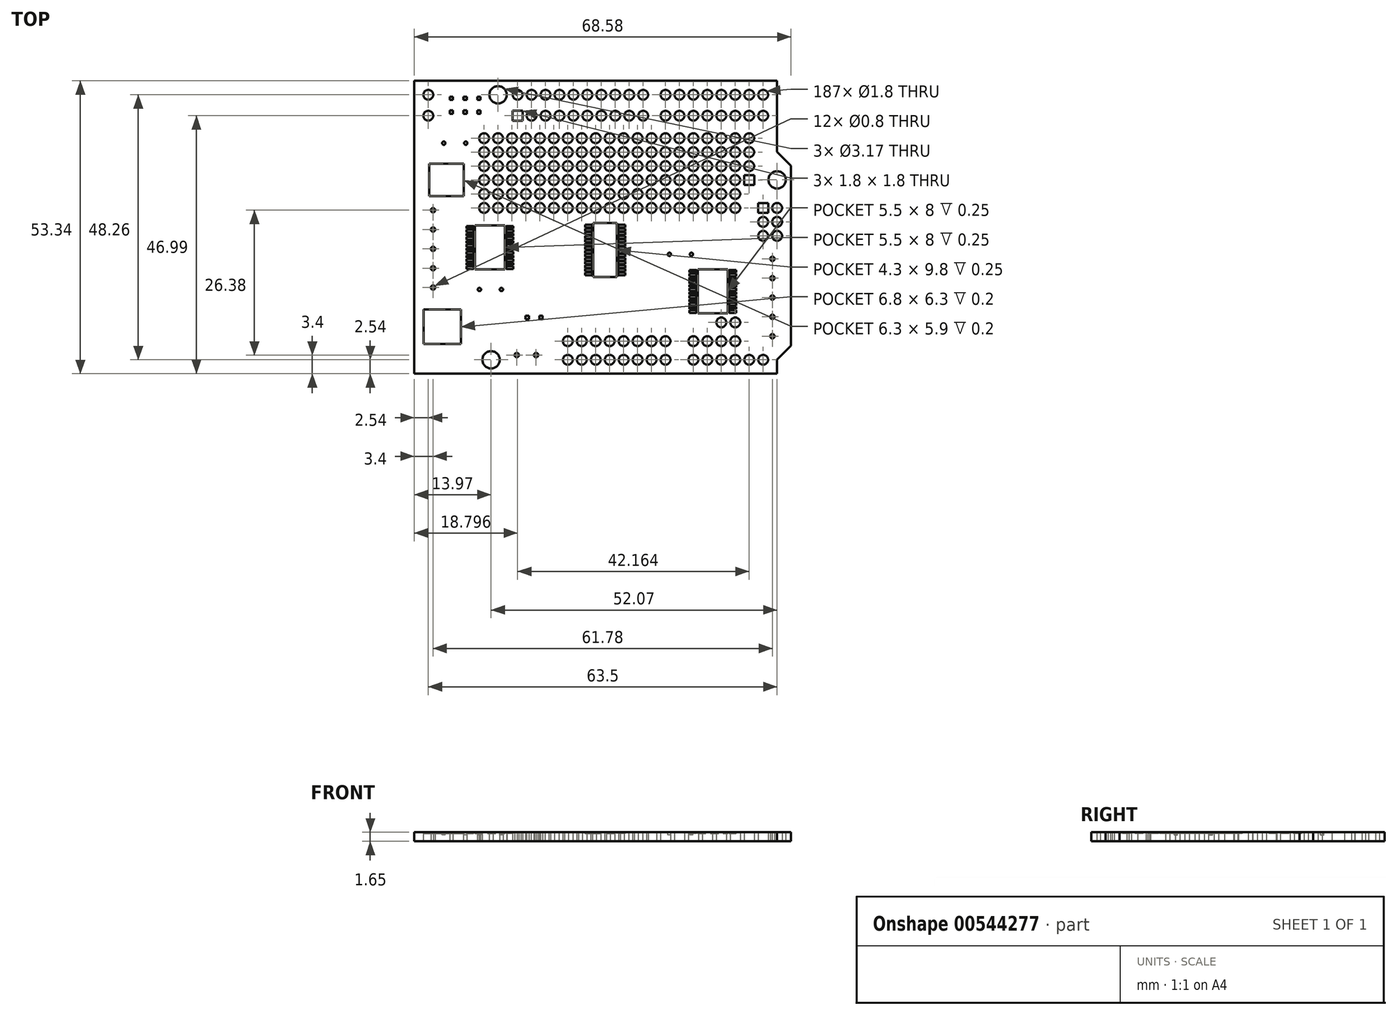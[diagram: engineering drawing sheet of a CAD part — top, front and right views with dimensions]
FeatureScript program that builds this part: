
annotation { "Feature Type Name" : "Feature", "Feature Type Description" : "" }
export const myFeature = defineFeature(function(context is Context, id is Id, definition is map)
    precondition{}
    {
        {
            var Q0;
            Q0=qCreatedBy(makeId("Top.planeOp"),FACE);
            var sketch = newSketch(context, id + "F0", { "sketchPlane" : qUnion([Q0])});
            skLineSegment(sketch, "E0.bottom", {"start": v(0, 0) * mm, "end": v(66.04, 0) * mm});
            skLineSegment(sketch, "E0.top", {"start": v(0, 53.34) * mm, "end": v(66.04, 53.34) * mm});
            skLineSegment(sketch, "E0.left", {"start": v(0, 0) * mm, "end": v(0, 53.34) * mm});
            skLineSegment(sketch, "E0.right", {"start": v(66.04, 0) * mm, "end": v(66.04, 2.54) * mm});
            skLineSegment(sketch, "E1", {"start": v(66.04, 40.39) * mm, "end": v(68.58, 37.85) * mm});
            skLineSegment(sketch, "E2", {"start": v(68.58, 37.85) * mm, "end": v(68.58, 5.08) * mm});
            skLineSegment(sketch, "E3", {"start": v(68.58, 5.08) * mm, "end": v(66.04, 2.54) * mm});
            skLineSegment(sketch, "E4.trimOffspring", {"start": v(66.04, 40.39) * mm, "end": v(66.04, 53.34) * mm});
            skCircle(sketch, "E5", {"center": v(15.24, 50.8) * mm, "radius": 1.59 * mm});
            skCircle(sketch, "E6", {"center": v(13.97, 2.54) * mm, "radius": 1.59 * mm});
            skCircle(sketch, "E7", {"center": v(66.04, 35.3) * mm, "radius": 1.59 * mm});
            skLineSegment(sketch, "E8", {"start": v(0, 50.8) * mm, "end": v(66.04, 50.8) * mm, "construction": true});
            skCircle(sketch, "E9", {"center": v(63.5, 50.8) * mm, "radius": 0.9 * mm});
            skCircle(sketch, "E10.1.0.0", {"center": v(60.96, 50.8) * mm, "radius": 0.9 * mm});
            skCircle(sketch, "E10.2.0.0", {"center": v(58.42, 50.8) * mm, "radius": 0.9 * mm});
            skCircle(sketch, "E10.3.0.0", {"center": v(55.88, 50.8) * mm, "radius": 0.9 * mm});
            skCircle(sketch, "E10.4.0.0", {"center": v(53.34, 50.8) * mm, "radius": 0.9 * mm});
            skCircle(sketch, "E10.5.0.0", {"center": v(50.8, 50.8) * mm, "radius": 0.9 * mm});
            skCircle(sketch, "E10.6.0.0", {"center": v(48.26, 50.8) * mm, "radius": 0.9 * mm});
            skCircle(sketch, "E10.7.0.0", {"center": v(45.72, 50.8) * mm, "radius": 0.9 * mm});
            skLineSegment(sketch, "E10.direction1", {"start": v(63.5, 50.8) * mm, "end": v(60.96, 50.8) * mm, "construction": true});
            skCircle(sketch, "E11", {"center": v(41.66, 50.8) * mm, "radius": 0.9 * mm});
            skCircle(sketch, "E12.1.0.0", {"center": v(39.12, 50.8) * mm, "radius": 0.9 * mm});
            skCircle(sketch, "E12.2.0.0", {"center": v(36.58, 50.8) * mm, "radius": 0.9 * mm});
            skCircle(sketch, "E12.3.0.0", {"center": v(34.04, 50.8) * mm, "radius": 0.9 * mm});
            skCircle(sketch, "E12.4.0.0", {"center": v(31.5, 50.8) * mm, "radius": 0.9 * mm});
            skCircle(sketch, "E12.5.0.0", {"center": v(28.96, 50.8) * mm, "radius": 0.9 * mm});
            skCircle(sketch, "E12.6.0.0", {"center": v(26.42, 50.8) * mm, "radius": 0.9 * mm});
            skCircle(sketch, "E12.7.0.0", {"center": v(23.88, 50.8) * mm, "radius": 0.9 * mm});
            skCircle(sketch, "E12.8.0.0", {"center": v(21.34, 50.8) * mm, "radius": 0.9 * mm});
            skCircle(sketch, "E12.9.0.0", {"center": v(18.8, 50.8) * mm, "radius": 0.9 * mm});
            skLineSegment(sketch, "E12.direction1", {"start": v(41.66, 50.8) * mm, "end": v(39.12, 50.8) * mm, "construction": true});
            skLineSegment(sketch, "E13", {"start": v(66.04, 2.54) * mm, "end": v(0, 2.54) * mm, "construction": true});
            skCircle(sketch, "E14", {"center": v(63.5, 2.54) * mm, "radius": 0.9 * mm});
            skCircle(sketch, "E15.1.0.0", {"center": v(60.96, 2.54) * mm, "radius": 0.9 * mm});
            skCircle(sketch, "E15.2.0.0", {"center": v(58.42, 2.54) * mm, "radius": 0.9 * mm});
            skCircle(sketch, "E15.3.0.0", {"center": v(55.88, 2.54) * mm, "radius": 0.9 * mm});
            skCircle(sketch, "E15.4.0.0", {"center": v(53.34, 2.54) * mm, "radius": 0.9 * mm});
            skCircle(sketch, "E15.5.0.0", {"center": v(50.8, 2.54) * mm, "radius": 0.9 * mm});
            skLineSegment(sketch, "E15.direction1", {"start": v(63.5, 2.54) * mm, "end": v(60.96, 2.54) * mm, "construction": true});
            skCircle(sketch, "E16", {"center": v(45.72, 2.54) * mm, "radius": 0.9 * mm});
            skCircle(sketch, "E17.1.0.0", {"center": v(43.18, 2.54) * mm, "radius": 0.9 * mm});
            skCircle(sketch, "E17.2.0.0", {"center": v(40.64, 2.54) * mm, "radius": 0.9 * mm});
            skCircle(sketch, "E17.3.0.0", {"center": v(38.1, 2.54) * mm, "radius": 0.9 * mm});
            skCircle(sketch, "E17.4.0.0", {"center": v(35.56, 2.54) * mm, "radius": 0.9 * mm});
            skCircle(sketch, "E17.5.0.0", {"center": v(33.02, 2.54) * mm, "radius": 0.9 * mm});
            skCircle(sketch, "E17.6.0.0", {"center": v(30.48, 2.54) * mm, "radius": 0.9 * mm});
            skCircle(sketch, "E17.7.0.0", {"center": v(27.94, 2.54) * mm, "radius": 0.9 * mm});
            skLineSegment(sketch, "E17.direction1", {"start": v(45.72, 2.54) * mm, "end": v(43.18, 2.54) * mm, "construction": true});
            skLineSegment(sketch, "E18", {"start": v(0, 46.99) * mm, "end": v(66.04, 46.99) * mm, "construction": true});
            skLineSegment(sketch, "E19.1.0.0", {"start": v(41.66, 46.99) * mm, "end": v(39.12, 46.99) * mm, "construction": true});
            skLineSegment(sketch, "E19.1.0.1", {"start": v(63.5, 46.99) * mm, "end": v(60.96, 46.99) * mm, "construction": true});
            skCircle(sketch, "E19.1.0.2", {"center": v(48.26, 46.99) * mm, "radius": 0.9 * mm});
            skCircle(sketch, "E19.1.0.3", {"center": v(31.5, 47) * mm, "radius": 0.9 * mm});
            skCircle(sketch, "E19.1.0.4", {"center": v(50.8, 46.99) * mm, "radius": 0.9 * mm});
            skCircle(sketch, "E19.1.0.6", {"center": v(34.04, 47) * mm, "radius": 0.9 * mm});
            skCircle(sketch, "E19.1.0.7", {"center": v(23.88, 47) * mm, "radius": 0.9 * mm});
            skCircle(sketch, "E19.1.0.8", {"center": v(53.34, 46.99) * mm, "radius": 0.9 * mm});
            skCircle(sketch, "E19.1.0.9", {"center": v(21.34, 46.99) * mm, "radius": 0.9 * mm});
            skCircle(sketch, "E19.1.0.10", {"center": v(36.58, 47) * mm, "radius": 0.9 * mm});
            skCircle(sketch, "E19.1.0.11", {"center": v(26.42, 47) * mm, "radius": 0.9 * mm});
            skCircle(sketch, "E19.1.0.12", {"center": v(55.88, 47) * mm, "radius": 0.9 * mm});
            skCircle(sketch, "E19.1.0.13", {"center": v(58.42, 47) * mm, "radius": 0.9 * mm});
            skCircle(sketch, "E19.1.0.14", {"center": v(45.72, 46.99) * mm, "radius": 0.9 * mm});
            skCircle(sketch, "E19.1.0.15", {"center": v(28.96, 47) * mm, "radius": 0.9 * mm});
            skCircle(sketch, "E19.1.0.16", {"center": v(39.12, 47) * mm, "radius": 0.9 * mm});
            skCircle(sketch, "E19.1.0.17", {"center": v(41.66, 47) * mm, "radius": 0.9 * mm});
            skCircle(sketch, "E19.1.0.18", {"center": v(63.5, 47) * mm, "radius": 0.9 * mm});
            skCircle(sketch, "E19.1.0.19", {"center": v(60.96, 47) * mm, "radius": 0.9 * mm});
            skLineSegment(sketch, "E19.direction1", {"start": v(18.8, 50.8) * mm, "end": v(18.8, 46.99) * mm, "construction": true});
            skLineSegment(sketch, "E20", {"start": v(68.58, 5.94) * mm, "end": v(0, 5.94) * mm, "construction": true});
            skLineSegment(sketch, "E21.1.0.0", {"start": v(45.72, 5.94) * mm, "end": v(43.18, 5.94) * mm, "construction": true});
            skCircle(sketch, "E21.1.0.1", {"center": v(55.88, 5.94) * mm, "radius": 0.9 * mm});
            skCircle(sketch, "E21.1.0.2", {"center": v(40.64, 5.94) * mm, "radius": 0.9 * mm});
            skCircle(sketch, "E21.1.0.3", {"center": v(58.42, 5.94) * mm, "radius": 0.9 * mm});
            skCircle(sketch, "E21.1.0.4", {"center": v(38.1, 5.94) * mm, "radius": 0.9 * mm});
            skCircle(sketch, "E21.1.0.5", {"center": v(30.48, 5.94) * mm, "radius": 0.9 * mm});
            skCircle(sketch, "E21.1.0.6", {"center": v(33.02, 5.94) * mm, "radius": 0.9 * mm});
            skCircle(sketch, "E21.1.0.7", {"center": v(50.8, 5.94) * mm, "radius": 0.9 * mm});
            skCircle(sketch, "E21.1.0.8", {"center": v(35.56, 5.94) * mm, "radius": 0.9 * mm});
            skCircle(sketch, "E21.1.0.9", {"center": v(53.34, 5.94) * mm, "radius": 0.9 * mm});
            skCircle(sketch, "E21.1.0.10", {"center": v(27.94, 5.94) * mm, "radius": 0.9 * mm});
            skCircle(sketch, "E21.1.0.11", {"center": v(43.18, 5.94) * mm, "radius": 0.9 * mm});
            skCircle(sketch, "E21.1.0.12", {"center": v(45.72, 5.94) * mm, "radius": 0.9 * mm});
            skLineSegment(sketch, "E21.direction1", {"start": v(27.94, 2.54) * mm, "end": v(27.94, 5.94) * mm, "construction": true});
            skLineSegment(sketch, "E22", {"start": v(58.42, 47) * mm, "end": v(58.42, 5.94) * mm, "construction": true});
            skLineSegment(sketch, "E23", {"start": v(0, 30.2) * mm, "end": v(66.04, 30.2) * mm, "construction": true});
            skLineSegment(sketch, "E24", {"start": v(0, 42.9) * mm, "end": v(66.04, 42.9) * mm, "construction": true});
            skCircle(sketch, "E25", {"center": v(58.42, 42.9) * mm, "radius": 0.9 * mm});
            skCircle(sketch, "E26", {"center": v(58.42, 30.2) * mm, "radius": 0.9 * mm});
            skCircle(sketch, "E27", {"center": v(58.42, 40.36) * mm, "radius": 0.9 * mm});
            skCircle(sketch, "E28", {"center": v(58.42, 37.82) * mm, "radius": 0.9 * mm});
            skCircle(sketch, "E29", {"center": v(58.42, 35.28) * mm, "radius": 0.9 * mm});
            skCircle(sketch, "E30", {"center": v(58.42, 32.74) * mm, "radius": 0.9 * mm});
            skCircle(sketch, "E31.1.0.0", {"center": v(55.88, 35.28) * mm, "radius": 0.9 * mm});
            skCircle(sketch, "E31.1.0.1", {"center": v(55.88, 32.74) * mm, "radius": 0.9 * mm});
            skCircle(sketch, "E31.1.0.2", {"center": v(55.88, 37.82) * mm, "radius": 0.9 * mm});
            skCircle(sketch, "E31.1.0.3", {"center": v(55.88, 40.36) * mm, "radius": 0.9 * mm});
            skCircle(sketch, "E31.1.0.4", {"center": v(55.88, 30.2) * mm, "radius": 0.9 * mm});
            skCircle(sketch, "E31.1.0.5", {"center": v(55.88, 42.9) * mm, "radius": 0.9 * mm});
            skCircle(sketch, "E31.2.0.0", {"center": v(53.34, 35.28) * mm, "radius": 0.9 * mm});
            skCircle(sketch, "E31.2.0.1", {"center": v(53.34, 32.74) * mm, "radius": 0.9 * mm});
            skCircle(sketch, "E31.2.0.2", {"center": v(53.34, 37.82) * mm, "radius": 0.9 * mm});
            skCircle(sketch, "E31.2.0.3", {"center": v(53.34, 40.36) * mm, "radius": 0.9 * mm});
            skCircle(sketch, "E31.2.0.4", {"center": v(53.34, 30.2) * mm, "radius": 0.9 * mm});
            skCircle(sketch, "E31.2.0.5", {"center": v(53.34, 42.9) * mm, "radius": 0.9 * mm});
            skCircle(sketch, "E31.3.0.0", {"center": v(50.8, 35.28) * mm, "radius": 0.9 * mm});
            skCircle(sketch, "E31.3.0.1", {"center": v(50.8, 32.74) * mm, "radius": 0.9 * mm});
            skCircle(sketch, "E31.3.0.2", {"center": v(50.8, 37.82) * mm, "radius": 0.9 * mm});
            skCircle(sketch, "E31.3.0.3", {"center": v(50.8, 40.36) * mm, "radius": 0.9 * mm});
            skCircle(sketch, "E31.3.0.4", {"center": v(50.8, 30.2) * mm, "radius": 0.9 * mm});
            skCircle(sketch, "E31.3.0.5", {"center": v(50.8, 42.9) * mm, "radius": 0.9 * mm});
            skCircle(sketch, "E31.4.0.0", {"center": v(48.26, 35.28) * mm, "radius": 0.9 * mm});
            skCircle(sketch, "E31.4.0.1", {"center": v(48.26, 32.74) * mm, "radius": 0.9 * mm});
            skCircle(sketch, "E31.4.0.2", {"center": v(48.26, 37.82) * mm, "radius": 0.9 * mm});
            skCircle(sketch, "E31.4.0.3", {"center": v(48.26, 40.36) * mm, "radius": 0.9 * mm});
            skCircle(sketch, "E31.4.0.4", {"center": v(48.26, 30.2) * mm, "radius": 0.9 * mm});
            skCircle(sketch, "E31.4.0.5", {"center": v(48.26, 42.9) * mm, "radius": 0.9 * mm});
            skCircle(sketch, "E31.5.0.0", {"center": v(45.72, 35.28) * mm, "radius": 0.9 * mm});
            skCircle(sketch, "E31.5.0.1", {"center": v(45.72, 32.74) * mm, "radius": 0.9 * mm});
            skCircle(sketch, "E31.5.0.2", {"center": v(45.72, 37.82) * mm, "radius": 0.9 * mm});
            skCircle(sketch, "E31.5.0.3", {"center": v(45.72, 40.36) * mm, "radius": 0.9 * mm});
            skCircle(sketch, "E31.5.0.4", {"center": v(45.72, 30.2) * mm, "radius": 0.9 * mm});
            skCircle(sketch, "E31.5.0.5", {"center": v(45.72, 42.9) * mm, "radius": 0.9 * mm});
            skCircle(sketch, "E31.6.0.0", {"center": v(43.18, 35.28) * mm, "radius": 0.9 * mm});
            skCircle(sketch, "E31.6.0.1", {"center": v(43.18, 32.74) * mm, "radius": 0.9 * mm});
            skCircle(sketch, "E31.6.0.2", {"center": v(43.18, 37.82) * mm, "radius": 0.9 * mm});
            skCircle(sketch, "E31.6.0.3", {"center": v(43.18, 40.36) * mm, "radius": 0.9 * mm});
            skCircle(sketch, "E31.6.0.4", {"center": v(43.18, 30.2) * mm, "radius": 0.9 * mm});
            skCircle(sketch, "E31.6.0.5", {"center": v(43.18, 42.9) * mm, "radius": 0.9 * mm});
            skCircle(sketch, "E31.7.0.0", {"center": v(40.64, 35.28) * mm, "radius": 0.9 * mm});
            skCircle(sketch, "E31.7.0.1", {"center": v(40.64, 32.74) * mm, "radius": 0.9 * mm});
            skCircle(sketch, "E31.7.0.2", {"center": v(40.64, 37.82) * mm, "radius": 0.9 * mm});
            skCircle(sketch, "E31.7.0.3", {"center": v(40.64, 40.36) * mm, "radius": 0.9 * mm});
            skCircle(sketch, "E31.7.0.4", {"center": v(40.64, 30.2) * mm, "radius": 0.9 * mm});
            skCircle(sketch, "E31.7.0.5", {"center": v(40.64, 42.9) * mm, "radius": 0.9 * mm});
            skCircle(sketch, "E31.8.0.0", {"center": v(38.1, 35.28) * mm, "radius": 0.9 * mm});
            skCircle(sketch, "E31.8.0.1", {"center": v(38.1, 32.74) * mm, "radius": 0.9 * mm});
            skCircle(sketch, "E31.8.0.2", {"center": v(38.1, 37.82) * mm, "radius": 0.9 * mm});
            skCircle(sketch, "E31.8.0.3", {"center": v(38.1, 40.36) * mm, "radius": 0.9 * mm});
            skCircle(sketch, "E31.8.0.4", {"center": v(38.1, 30.2) * mm, "radius": 0.9 * mm});
            skCircle(sketch, "E31.8.0.5", {"center": v(38.1, 42.9) * mm, "radius": 0.9 * mm});
            skCircle(sketch, "E31.9.0.0", {"center": v(35.56, 35.28) * mm, "radius": 0.9 * mm});
            skCircle(sketch, "E31.9.0.1", {"center": v(35.56, 32.74) * mm, "radius": 0.9 * mm});
            skCircle(sketch, "E31.9.0.2", {"center": v(35.56, 37.82) * mm, "radius": 0.9 * mm});
            skCircle(sketch, "E31.9.0.3", {"center": v(35.56, 40.36) * mm, "radius": 0.9 * mm});
            skCircle(sketch, "E31.9.0.4", {"center": v(35.56, 30.2) * mm, "radius": 0.9 * mm});
            skCircle(sketch, "E31.9.0.5", {"center": v(35.56, 42.9) * mm, "radius": 0.9 * mm});
            skCircle(sketch, "E31.10.0.0", {"center": v(33.02, 35.28) * mm, "radius": 0.9 * mm});
            skCircle(sketch, "E31.10.0.1", {"center": v(33.02, 32.74) * mm, "radius": 0.9 * mm});
            skCircle(sketch, "E31.10.0.2", {"center": v(33.02, 37.82) * mm, "radius": 0.9 * mm});
            skCircle(sketch, "E31.10.0.3", {"center": v(33.02, 40.36) * mm, "radius": 0.9 * mm});
            skCircle(sketch, "E31.10.0.4", {"center": v(33.02, 30.2) * mm, "radius": 0.9 * mm});
            skCircle(sketch, "E31.10.0.5", {"center": v(33.02, 42.9) * mm, "radius": 0.9 * mm});
            skCircle(sketch, "E31.11.0.0", {"center": v(30.48, 35.28) * mm, "radius": 0.9 * mm});
            skCircle(sketch, "E31.11.0.1", {"center": v(30.48, 32.74) * mm, "radius": 0.9 * mm});
            skCircle(sketch, "E31.11.0.2", {"center": v(30.48, 37.82) * mm, "radius": 0.9 * mm});
            skCircle(sketch, "E31.11.0.3", {"center": v(30.48, 40.36) * mm, "radius": 0.9 * mm});
            skCircle(sketch, "E31.11.0.4", {"center": v(30.48, 30.2) * mm, "radius": 0.9 * mm});
            skCircle(sketch, "E31.11.0.5", {"center": v(30.48, 42.9) * mm, "radius": 0.9 * mm});
            skCircle(sketch, "E31.12.0.0", {"center": v(27.94, 35.28) * mm, "radius": 0.9 * mm});
            skCircle(sketch, "E31.12.0.1", {"center": v(27.94, 32.74) * mm, "radius": 0.9 * mm});
            skCircle(sketch, "E31.12.0.2", {"center": v(27.94, 37.82) * mm, "radius": 0.9 * mm});
            skCircle(sketch, "E31.12.0.3", {"center": v(27.94, 40.36) * mm, "radius": 0.9 * mm});
            skCircle(sketch, "E31.12.0.4", {"center": v(27.94, 30.2) * mm, "radius": 0.9 * mm});
            skCircle(sketch, "E31.12.0.5", {"center": v(27.94, 42.9) * mm, "radius": 0.9 * mm});
            skCircle(sketch, "E31.13.0.0", {"center": v(25.4, 35.28) * mm, "radius": 0.9 * mm});
            skCircle(sketch, "E31.13.0.1", {"center": v(25.4, 32.74) * mm, "radius": 0.9 * mm});
            skCircle(sketch, "E31.13.0.2", {"center": v(25.4, 37.82) * mm, "radius": 0.9 * mm});
            skCircle(sketch, "E31.13.0.3", {"center": v(25.4, 40.36) * mm, "radius": 0.9 * mm});
            skCircle(sketch, "E31.13.0.4", {"center": v(25.4, 30.2) * mm, "radius": 0.9 * mm});
            skCircle(sketch, "E31.13.0.5", {"center": v(25.4, 42.9) * mm, "radius": 0.9 * mm});
            skCircle(sketch, "E31.14.0.0", {"center": v(22.86, 35.28) * mm, "radius": 0.9 * mm});
            skCircle(sketch, "E31.14.0.1", {"center": v(22.86, 32.74) * mm, "radius": 0.9 * mm});
            skCircle(sketch, "E31.14.0.2", {"center": v(22.86, 37.82) * mm, "radius": 0.9 * mm});
            skCircle(sketch, "E31.14.0.3", {"center": v(22.86, 40.36) * mm, "radius": 0.9 * mm});
            skCircle(sketch, "E31.14.0.4", {"center": v(22.86, 30.2) * mm, "radius": 0.9 * mm});
            skCircle(sketch, "E31.14.0.5", {"center": v(22.86, 42.9) * mm, "radius": 0.9 * mm});
            skCircle(sketch, "E31.15.0.0", {"center": v(20.32, 35.28) * mm, "radius": 0.9 * mm});
            skCircle(sketch, "E31.15.0.1", {"center": v(20.32, 32.74) * mm, "radius": 0.9 * mm});
            skCircle(sketch, "E31.15.0.2", {"center": v(20.32, 37.82) * mm, "radius": 0.9 * mm});
            skCircle(sketch, "E31.15.0.3", {"center": v(20.32, 40.36) * mm, "radius": 0.9 * mm});
            skCircle(sketch, "E31.15.0.4", {"center": v(20.32, 30.2) * mm, "radius": 0.9 * mm});
            skCircle(sketch, "E31.15.0.5", {"center": v(20.32, 42.9) * mm, "radius": 0.9 * mm});
            skCircle(sketch, "E31.16.0.0", {"center": v(17.78, 35.28) * mm, "radius": 0.9 * mm});
            skCircle(sketch, "E31.16.0.1", {"center": v(17.78, 32.74) * mm, "radius": 0.9 * mm});
            skCircle(sketch, "E31.16.0.2", {"center": v(17.78, 37.82) * mm, "radius": 0.9 * mm});
            skCircle(sketch, "E31.16.0.3", {"center": v(17.78, 40.36) * mm, "radius": 0.9 * mm});
            skCircle(sketch, "E31.16.0.4", {"center": v(17.78, 30.2) * mm, "radius": 0.9 * mm});
            skCircle(sketch, "E31.16.0.5", {"center": v(17.78, 42.9) * mm, "radius": 0.9 * mm});
            skCircle(sketch, "E31.17.0.0", {"center": v(15.24, 35.28) * mm, "radius": 0.9 * mm});
            skCircle(sketch, "E31.17.0.1", {"center": v(15.24, 32.74) * mm, "radius": 0.9 * mm});
            skCircle(sketch, "E31.17.0.2", {"center": v(15.24, 37.82) * mm, "radius": 0.9 * mm});
            skCircle(sketch, "E31.17.0.3", {"center": v(15.24, 40.36) * mm, "radius": 0.9 * mm});
            skCircle(sketch, "E31.17.0.4", {"center": v(15.24, 30.2) * mm, "radius": 0.9 * mm});
            skCircle(sketch, "E31.17.0.5", {"center": v(15.24, 42.9) * mm, "radius": 0.9 * mm});
            skCircle(sketch, "E31.18.0.0", {"center": v(12.7, 35.28) * mm, "radius": 0.9 * mm});
            skCircle(sketch, "E31.18.0.1", {"center": v(12.7, 32.74) * mm, "radius": 0.9 * mm});
            skCircle(sketch, "E31.18.0.2", {"center": v(12.7, 37.82) * mm, "radius": 0.9 * mm});
            skCircle(sketch, "E31.18.0.3", {"center": v(12.7, 40.36) * mm, "radius": 0.9 * mm});
            skCircle(sketch, "E31.18.0.4", {"center": v(12.7, 30.2) * mm, "radius": 0.9 * mm});
            skCircle(sketch, "E31.18.0.5", {"center": v(12.7, 42.9) * mm, "radius": 0.9 * mm});
            skLineSegment(sketch, "E31.direction1", {"start": v(58.42, 30.2) * mm, "end": v(55.88, 30.2) * mm, "construction": true});
            skCircle(sketch, "E32", {"center": v(60.96, 42.9) * mm, "radius": 0.9 * mm});
            skCircle(sketch, "E33", {"center": v(60.96, 40.36) * mm, "radius": 0.9 * mm});
            skCircle(sketch, "E34", {"center": v(60.96, 37.82) * mm, "radius": 0.9 * mm});
            skLineSegment(sketch, "E35", {"start": v(66.04, 40.39) * mm, "end": v(66.04, 2.54) * mm, "construction": true});
            skCircle(sketch, "E36", {"center": v(66.04, 25.12) * mm, "radius": 0.9 * mm});
            skCircle(sketch, "E37", {"center": v(66.04, 30.2) * mm, "radius": 0.9 * mm});
            skCircle(sketch, "E38", {"center": v(66.04, 27.66) * mm, "radius": 0.9 * mm});
            skCircle(sketch, "E39", {"center": v(63.5, 27.66) * mm, "radius": 0.9 * mm});
            skCircle(sketch, "E40", {"center": v(63.5, 25.12) * mm, "radius": 0.9 * mm});
            skCircle(sketch, "E41", {"center": v(58.42, 9.34) * mm, "radius": 0.9 * mm});
            skCircle(sketch, "E42", {"center": v(55.88, 9.34) * mm, "radius": 0.9 * mm});
            skCircle(sketch, "E43", {"center": v(2.54, 50.8) * mm, "radius": 0.9 * mm});
            skCircle(sketch, "E44", {"center": v(2.54, 46.99) * mm, "radius": 0.9 * mm});
            skLineSegment(sketch, "E45.bottom", {"start": v(17.9, 47.9) * mm, "end": v(19.7, 47.9) * mm});
            skLineSegment(sketch, "E45.top", {"start": v(17.9, 46.1) * mm, "end": v(19.7, 46.1) * mm});
            skLineSegment(sketch, "E45.left", {"start": v(17.9, 47.9) * mm, "end": v(17.9, 46.1) * mm});
            skLineSegment(sketch, "E45.right", {"start": v(19.7, 47.9) * mm, "end": v(19.7, 46.1) * mm});
            skLineSegment(sketch, "E46.bottom", {"start": v(60.06, 36.18) * mm, "end": v(61.86, 36.18) * mm});
            skLineSegment(sketch, "E46.top", {"start": v(60.06, 34.38) * mm, "end": v(61.86, 34.38) * mm});
            skLineSegment(sketch, "E46.left", {"start": v(60.06, 36.18) * mm, "end": v(60.06, 34.38) * mm});
            skLineSegment(sketch, "E46.right", {"start": v(61.86, 36.18) * mm, "end": v(61.86, 34.38) * mm});
            skLineSegment(sketch, "E47.bottom", {"start": v(62.6, 31.1) * mm, "end": v(64.4, 31.1) * mm});
            skLineSegment(sketch, "E47.top", {"start": v(62.6, 29.3) * mm, "end": v(64.4, 29.3) * mm});
            skLineSegment(sketch, "E47.left", {"start": v(62.6, 31.1) * mm, "end": v(62.6, 29.3) * mm});
            skLineSegment(sketch, "E47.right", {"start": v(64.4, 31.1) * mm, "end": v(64.4, 29.3) * mm});
            skLineSegment(sketch, "E48", {"start": v(68.58, 5.08) * mm, "end": v(61.78, 5.08) * mm, "construction": true});
            skLineSegment(sketch, "E49", {"start": v(61.78, 5.08) * mm, "end": v(61.78, 22.68) * mm, "construction": true});
            skLineSegment(sketch, "E50", {"start": v(61.78, 22.68) * mm, "end": v(68.58, 22.68) * mm, "construction": true});
            skLineSegment(sketch, "E51", {"start": v(61.78, 20.92) * mm, "end": v(68.58, 20.92) * mm, "construction": true});
            skLineSegment(sketch, "E52", {"start": v(61.78, 17.4) * mm, "end": v(68.58, 17.4) * mm, "construction": true});
            skLineSegment(sketch, "E53", {"start": v(61.78, 13.88) * mm, "end": v(68.58, 13.88) * mm, "construction": true});
            skLineSegment(sketch, "E54", {"start": v(61.78, 10.36) * mm, "end": v(68.58, 10.36) * mm, "construction": true});
            skLineSegment(sketch, "E55", {"start": v(61.78, 6.84) * mm, "end": v(68.58, 6.84) * mm, "construction": true});
            skCircle(sketch, "E56", {"center": v(65.18, 17.4) * mm, "radius": 0.4 * mm});
            skCircle(sketch, "E57", {"center": v(65.18, 20.92) * mm, "radius": 0.4 * mm});
            skCircle(sketch, "E58", {"center": v(65.18, 13.88) * mm, "radius": 0.4 * mm});
            skCircle(sketch, "E59", {"center": v(65.18, 10.36) * mm, "radius": 0.4 * mm});
            skCircle(sketch, "E60", {"center": v(65.18, 6.84) * mm, "radius": 0.4 * mm});
            skLineSegment(sketch, "E61", {"start": v(0, 31.54) * mm, "end": v(6.8, 31.54) * mm, "construction": true});
            skLineSegment(sketch, "E62", {"start": v(6.8, 31.54) * mm, "end": v(6.8, 13.94) * mm, "construction": true});
            skLineSegment(sketch, "E63", {"start": v(6.8, 13.94) * mm, "end": v(0, 13.94) * mm, "construction": true});
            skLineSegment(sketch, "E64", {"start": v(0, 29.78) * mm, "end": v(6.8, 29.78) * mm, "construction": true});
            skLineSegment(sketch, "E65", {"start": v(0, 26.26) * mm, "end": v(6.8, 26.26) * mm, "construction": true});
            skLineSegment(sketch, "E66", {"start": v(0, 22.74) * mm, "end": v(6.8, 22.74) * mm, "construction": true});
            skLineSegment(sketch, "E67", {"start": v(0, 19.22) * mm, "end": v(6.8, 19.22) * mm, "construction": true});
            skLineSegment(sketch, "E68", {"start": v(0, 15.7) * mm, "end": v(6.8, 15.7) * mm, "construction": true});
            skCircle(sketch, "E69", {"center": v(3.4, 29.78) * mm, "radius": 0.4 * mm});
            skCircle(sketch, "E70", {"center": v(3.4, 26.26) * mm, "radius": 0.4 * mm});
            skCircle(sketch, "E71", {"center": v(3.4, 22.74) * mm, "radius": 0.4 * mm});
            skCircle(sketch, "E72", {"center": v(3.4, 19.22) * mm, "radius": 0.4 * mm});
            skCircle(sketch, "E73", {"center": v(3.4, 15.7) * mm, "radius": 0.4 * mm});
            skLineSegment(sketch, "E74", {"start": v(16.88, 0) * mm, "end": v(16.88, 6.8) * mm, "construction": true});
            skLineSegment(sketch, "E75", {"start": v(16.88, 6.8) * mm, "end": v(23.92, 6.8) * mm, "construction": true});
            skLineSegment(sketch, "E76", {"start": v(23.92, 6.8) * mm, "end": v(23.92, 0) * mm, "construction": true});
            skLineSegment(sketch, "E77", {"start": v(18.64, 6.8) * mm, "end": v(18.64, 0) * mm, "construction": true});
            skLineSegment(sketch, "E78", {"start": v(22.16, 6.8) * mm, "end": v(22.16, 0) * mm, "construction": true});
            skCircle(sketch, "E79", {"center": v(18.64, 3.4) * mm, "radius": 0.4 * mm});
            skCircle(sketch, "E80", {"center": v(22.16, 3.4) * mm, "radius": 0.4 * mm});
            skLineSegment(sketch, "E81.bottom", {"start": v(5.5, 51.4) * mm, "end": v(13, 51.4) * mm, "construction": true});
            skLineSegment(sketch, "E81.top", {"start": v(5.5, 46.4) * mm, "end": v(13, 46.4) * mm, "construction": true});
            skLineSegment(sketch, "E81.left", {"start": v(5.5, 51.4) * mm, "end": v(5.5, 46.4) * mm, "construction": true});
            skLineSegment(sketch, "E81.right", {"start": v(13, 51.4) * mm, "end": v(13, 46.4) * mm, "construction": true});
            skLineSegment(sketch, "E82", {"start": v(6.75, 51.4) * mm, "end": v(6.75, 46.4) * mm, "construction": true});
            skLineSegment(sketch, "E83", {"start": v(11.75, 51.4) * mm, "end": v(11.75, 46.4) * mm, "construction": true});
            skLineSegment(sketch, "E84", {"start": v(9.25, 51.4) * mm, "end": v(9.25, 46.4) * mm, "construction": true});
            skLineSegment(sketch, "E85.bottom", {"start": v(6.45, 50.45) * mm, "end": v(7.05, 50.45) * mm});
            skLineSegment(sketch, "E85.top", {"start": v(6.45, 49.84) * mm, "end": v(7.05, 49.84) * mm});
            skLineSegment(sketch, "E85.left", {"start": v(6.45, 50.45) * mm, "end": v(6.45, 49.84) * mm});
            skLineSegment(sketch, "E85.right", {"start": v(7.05, 50.45) * mm, "end": v(7.05, 49.84) * mm});
            skLineSegment(sketch, "E86.bottom", {"start": v(8.95, 50.45) * mm, "end": v(9.55, 50.45) * mm});
            skLineSegment(sketch, "E86.top", {"start": v(8.95, 49.84) * mm, "end": v(9.55, 49.84) * mm});
            skLineSegment(sketch, "E86.left", {"start": v(8.95, 50.45) * mm, "end": v(8.95, 49.84) * mm});
            skLineSegment(sketch, "E86.right", {"start": v(9.55, 50.45) * mm, "end": v(9.55, 49.84) * mm});
            skLineSegment(sketch, "E87.bottom", {"start": v(11.45, 50.45) * mm, "end": v(12.05, 50.45) * mm});
            skLineSegment(sketch, "E87.top", {"start": v(11.45, 49.84) * mm, "end": v(12.05, 49.84) * mm});
            skLineSegment(sketch, "E87.left", {"start": v(11.45, 50.45) * mm, "end": v(11.45, 49.84) * mm});
            skLineSegment(sketch, "E87.right", {"start": v(12.05, 50.45) * mm, "end": v(12.05, 49.84) * mm});
            skLineSegment(sketch, "E88.bottom", {"start": v(6.45, 47.95) * mm, "end": v(7.05, 47.95) * mm});
            skLineSegment(sketch, "E88.top", {"start": v(6.45, 47.34) * mm, "end": v(7.05, 47.34) * mm});
            skLineSegment(sketch, "E88.left", {"start": v(6.45, 47.95) * mm, "end": v(6.45, 47.34) * mm});
            skLineSegment(sketch, "E88.right", {"start": v(7.05, 47.95) * mm, "end": v(7.05, 47.34) * mm});
            skLineSegment(sketch, "E89.bottom", {"start": v(8.95, 47.95) * mm, "end": v(9.55, 47.95) * mm});
            skLineSegment(sketch, "E89.top", {"start": v(8.95, 47.35) * mm, "end": v(9.55, 47.35) * mm});
            skLineSegment(sketch, "E89.left", {"start": v(8.95, 47.95) * mm, "end": v(8.95, 47.34) * mm});
            skLineSegment(sketch, "E89.right", {"start": v(9.55, 47.95) * mm, "end": v(9.55, 47.34) * mm});
            skLineSegment(sketch, "E90.bottom", {"start": v(11.45, 47.95) * mm, "end": v(12.05, 47.95) * mm});
            skLineSegment(sketch, "E90.top", {"start": v(11.45, 47.35) * mm, "end": v(12.05, 47.35) * mm});
            skLineSegment(sketch, "E90.left", {"start": v(11.45, 47.95) * mm, "end": v(11.45, 47.35) * mm});
            skLineSegment(sketch, "E90.right", {"start": v(12.05, 47.95) * mm, "end": v(12.05, 47.35) * mm});
            skLineSegment(sketch, "E91.bottom", {"start": v(19.3, 11.5) * mm, "end": v(24.3, 11.5) * mm, "construction": true});
            skLineSegment(sketch, "E91.top", {"start": v(19.3, 9) * mm, "end": v(24.3, 9) * mm, "construction": true});
            skLineSegment(sketch, "E91.left", {"start": v(19.3, 11.5) * mm, "end": v(19.3, 9) * mm, "construction": true});
            skLineSegment(sketch, "E91.right", {"start": v(24.3, 11.5) * mm, "end": v(24.3, 9) * mm, "construction": true});
            skLineSegment(sketch, "E92.bottom", {"start": v(20.25, 10.55) * mm, "end": v(20.85, 10.55) * mm});
            skLineSegment(sketch, "E92.top", {"start": v(20.25, 9.95) * mm, "end": v(20.85, 9.95) * mm});
            skLineSegment(sketch, "E92.left", {"start": v(20.25, 10.55) * mm, "end": v(20.25, 9.95) * mm});
            skLineSegment(sketch, "E92.right", {"start": v(20.85, 10.55) * mm, "end": v(20.85, 9.95) * mm});
            skLineSegment(sketch, "E93.bottom", {"start": v(22.75, 10.55) * mm, "end": v(23.35, 10.55) * mm});
            skLineSegment(sketch, "E93.top", {"start": v(22.75, 9.95) * mm, "end": v(23.35, 9.95) * mm});
            skLineSegment(sketch, "E93.left", {"start": v(22.75, 10.55) * mm, "end": v(22.75, 9.95) * mm});
            skLineSegment(sketch, "E93.right", {"start": v(23.35, 10.55) * mm, "end": v(23.35, 9.95) * mm});
            skSolve(sketch);
        }
        {
            var Q0;
            Q0=qSketchRegion(id+"F0",true);
            extrude(context, id + "F1", {"entities" : qUnion([Q0]), "depth" : 1.65 * mm});
        }
        {
            var Q0;
            Q0=makeQuery(id+"F1.opExtrude","CAP_FACE",FACE,{"disambiguationData":[OSD([sQuery(id+"F0.wireOp",EDGE,"E0.bottom"),sQuery(id+"F0.wireOp",EDGE,"E0.top"),sQuery(id+"F0.wireOp",EDGE,"E0.left"),sQuery(id+"F0.wireOp",EDGE,"E0.right"),sQuery(id+"F0.wireOp",EDGE,"E1"),sQuery(id+"F0.wireOp",EDGE,"E2"),sQuery(id+"F0.wireOp",EDGE,"E3"),sQuery(id+"F0.wireOp",EDGE,"E4.trimOffspring"),sQuery(id+"F0.wireOp",EDGE,"E5"),sQuery(id+"F0.wireOp",EDGE,"E6"),sQuery(id+"F0.wireOp",EDGE,"E7"),sQuery(id+"F0.wireOp",EDGE,"E9"),sQuery(id+"F0.wireOp",EDGE,"E10.1.0.0"),sQuery(id+"F0.wireOp",EDGE,"E10.2.0.0"),sQuery(id+"F0.wireOp",EDGE,"E10.3.0.0"),sQuery(id+"F0.wireOp",EDGE,"E10.4.0.0"),sQuery(id+"F0.wireOp",EDGE,"E10.5.0.0"),sQuery(id+"F0.wireOp",EDGE,"E10.6.0.0"),sQuery(id+"F0.wireOp",EDGE,"E10.7.0.0"),sQuery(id+"F0.wireOp",EDGE,"E11"),sQuery(id+"F0.wireOp",EDGE,"E12.1.0.0"),sQuery(id+"F0.wireOp",EDGE,"E12.2.0.0"),sQuery(id+"F0.wireOp",EDGE,"E12.3.0.0"),sQuery(id+"F0.wireOp",EDGE,"E12.4.0.0"),sQuery(id+"F0.wireOp",EDGE,"E12.5.0.0"),sQuery(id+"F0.wireOp",EDGE,"E12.6.0.0"),sQuery(id+"F0.wireOp",EDGE,"E12.7.0.0"),sQuery(id+"F0.wireOp",EDGE,"E12.8.0.0"),sQuery(id+"F0.wireOp",EDGE,"E12.9.0.0"),sQuery(id+"F0.wireOp",EDGE,"E14"),sQuery(id+"F0.wireOp",EDGE,"E15.1.0.0"),sQuery(id+"F0.wireOp",EDGE,"E15.2.0.0"),sQuery(id+"F0.wireOp",EDGE,"E15.3.0.0"),sQuery(id+"F0.wireOp",EDGE,"E15.4.0.0"),sQuery(id+"F0.wireOp",EDGE,"E15.5.0.0"),sQuery(id+"F0.wireOp",EDGE,"E16"),sQuery(id+"F0.wireOp",EDGE,"E17.1.0.0"),sQuery(id+"F0.wireOp",EDGE,"E17.2.0.0"),sQuery(id+"F0.wireOp",EDGE,"E17.3.0.0"),sQuery(id+"F0.wireOp",EDGE,"E17.4.0.0"),sQuery(id+"F0.wireOp",EDGE,"E17.5.0.0"),sQuery(id+"F0.wireOp",EDGE,"E17.6.0.0"),sQuery(id+"F0.wireOp",EDGE,"E17.7.0.0"),sQuery(id+"F0.wireOp",EDGE,"E19.1.0.2"),sQuery(id+"F0.wireOp",EDGE,"E19.1.0.3"),sQuery(id+"F0.wireOp",EDGE,"E19.1.0.4"),sQuery(id+"F0.wireOp",EDGE,"E19.1.0.6"),sQuery(id+"F0.wireOp",EDGE,"E19.1.0.7"),sQuery(id+"F0.wireOp",EDGE,"E19.1.0.8"),sQuery(id+"F0.wireOp",EDGE,"E19.1.0.9"),sQuery(id+"F0.wireOp",EDGE,"E19.1.0.10"),sQuery(id+"F0.wireOp",EDGE,"E19.1.0.11"),sQuery(id+"F0.wireOp",EDGE,"E19.1.0.12"),sQuery(id+"F0.wireOp",EDGE,"E19.1.0.13"),sQuery(id+"F0.wireOp",EDGE,"E19.1.0.14"),sQuery(id+"F0.wireOp",EDGE,"E19.1.0.15"),sQuery(id+"F0.wireOp",EDGE,"E19.1.0.16"),sQuery(id+"F0.wireOp",EDGE,"E19.1.0.17"),sQuery(id+"F0.wireOp",EDGE,"E19.1.0.18"),sQuery(id+"F0.wireOp",EDGE,"E19.1.0.19"),sQuery(id+"F0.wireOp",EDGE,"E21.1.0.1"),sQuery(id+"F0.wireOp",EDGE,"E21.1.0.2"),sQuery(id+"F0.wireOp",EDGE,"E21.1.0.3"),sQuery(id+"F0.wireOp",EDGE,"E21.1.0.4"),sQuery(id+"F0.wireOp",EDGE,"E21.1.0.5"),sQuery(id+"F0.wireOp",EDGE,"E21.1.0.6"),sQuery(id+"F0.wireOp",EDGE,"E21.1.0.7"),sQuery(id+"F0.wireOp",EDGE,"E21.1.0.8"),sQuery(id+"F0.wireOp",EDGE,"E21.1.0.9"),sQuery(id+"F0.wireOp",EDGE,"E21.1.0.10"),sQuery(id+"F0.wireOp",EDGE,"E21.1.0.11"),sQuery(id+"F0.wireOp",EDGE,"E21.1.0.12"),sQuery(id+"F0.wireOp",EDGE,"E25"),sQuery(id+"F0.wireOp",EDGE,"E26"),sQuery(id+"F0.wireOp",EDGE,"E27"),sQuery(id+"F0.wireOp",EDGE,"E28"),sQuery(id+"F0.wireOp",EDGE,"E29"),sQuery(id+"F0.wireOp",EDGE,"E30"),sQuery(id+"F0.wireOp",EDGE,"E31.1.0.0"),sQuery(id+"F0.wireOp",EDGE,"E31.1.0.1"),sQuery(id+"F0.wireOp",EDGE,"E31.1.0.2"),sQuery(id+"F0.wireOp",EDGE,"E31.1.0.3"),sQuery(id+"F0.wireOp",EDGE,"E31.1.0.4"),sQuery(id+"F0.wireOp",EDGE,"E31.1.0.5"),sQuery(id+"F0.wireOp",EDGE,"E31.2.0.0"),sQuery(id+"F0.wireOp",EDGE,"E31.2.0.1"),sQuery(id+"F0.wireOp",EDGE,"E31.2.0.2"),sQuery(id+"F0.wireOp",EDGE,"E31.2.0.3"),sQuery(id+"F0.wireOp",EDGE,"E31.2.0.4"),sQuery(id+"F0.wireOp",EDGE,"E31.2.0.5"),sQuery(id+"F0.wireOp",EDGE,"E31.3.0.0"),sQuery(id+"F0.wireOp",EDGE,"E31.3.0.1"),sQuery(id+"F0.wireOp",EDGE,"E31.3.0.2"),sQuery(id+"F0.wireOp",EDGE,"E31.3.0.3"),sQuery(id+"F0.wireOp",EDGE,"E31.3.0.4"),sQuery(id+"F0.wireOp",EDGE,"E31.3.0.5"),sQuery(id+"F0.wireOp",EDGE,"E31.4.0.0"),sQuery(id+"F0.wireOp",EDGE,"E31.4.0.1"),sQuery(id+"F0.wireOp",EDGE,"E31.4.0.2"),sQuery(id+"F0.wireOp",EDGE,"E31.4.0.3"),sQuery(id+"F0.wireOp",EDGE,"E31.4.0.4"),sQuery(id+"F0.wireOp",EDGE,"E31.4.0.5"),sQuery(id+"F0.wireOp",EDGE,"E31.5.0.0"),sQuery(id+"F0.wireOp",EDGE,"E31.5.0.1"),sQuery(id+"F0.wireOp",EDGE,"E31.5.0.2"),sQuery(id+"F0.wireOp",EDGE,"E31.5.0.3"),sQuery(id+"F0.wireOp",EDGE,"E31.5.0.4"),sQuery(id+"F0.wireOp",EDGE,"E31.5.0.5"),sQuery(id+"F0.wireOp",EDGE,"E31.6.0.0"),sQuery(id+"F0.wireOp",EDGE,"E31.6.0.1"),sQuery(id+"F0.wireOp",EDGE,"E31.6.0.2"),sQuery(id+"F0.wireOp",EDGE,"E31.6.0.3"),sQuery(id+"F0.wireOp",EDGE,"E31.6.0.4"),sQuery(id+"F0.wireOp",EDGE,"E31.6.0.5"),sQuery(id+"F0.wireOp",EDGE,"E31.7.0.0"),sQuery(id+"F0.wireOp",EDGE,"E31.7.0.1"),sQuery(id+"F0.wireOp",EDGE,"E31.7.0.2"),sQuery(id+"F0.wireOp",EDGE,"E31.7.0.3"),sQuery(id+"F0.wireOp",EDGE,"E31.7.0.4"),sQuery(id+"F0.wireOp",EDGE,"E31.7.0.5"),sQuery(id+"F0.wireOp",EDGE,"E31.8.0.0"),sQuery(id+"F0.wireOp",EDGE,"E31.8.0.1"),sQuery(id+"F0.wireOp",EDGE,"E31.8.0.2"),sQuery(id+"F0.wireOp",EDGE,"E31.8.0.3"),sQuery(id+"F0.wireOp",EDGE,"E31.8.0.4"),sQuery(id+"F0.wireOp",EDGE,"E31.8.0.5"),sQuery(id+"F0.wireOp",EDGE,"E31.9.0.0"),sQuery(id+"F0.wireOp",EDGE,"E31.9.0.1"),sQuery(id+"F0.wireOp",EDGE,"E31.9.0.2"),sQuery(id+"F0.wireOp",EDGE,"E31.9.0.3"),sQuery(id+"F0.wireOp",EDGE,"E31.9.0.4"),sQuery(id+"F0.wireOp",EDGE,"E31.9.0.5"),sQuery(id+"F0.wireOp",EDGE,"E31.10.0.0"),sQuery(id+"F0.wireOp",EDGE,"E31.10.0.1"),sQuery(id+"F0.wireOp",EDGE,"E31.10.0.2"),sQuery(id+"F0.wireOp",EDGE,"E31.10.0.3"),sQuery(id+"F0.wireOp",EDGE,"E31.10.0.4"),sQuery(id+"F0.wireOp",EDGE,"E31.10.0.5"),sQuery(id+"F0.wireOp",EDGE,"E31.11.0.0"),sQuery(id+"F0.wireOp",EDGE,"E31.11.0.1"),sQuery(id+"F0.wireOp",EDGE,"E31.11.0.2"),sQuery(id+"F0.wireOp",EDGE,"E31.11.0.3"),sQuery(id+"F0.wireOp",EDGE,"E31.11.0.4"),sQuery(id+"F0.wireOp",EDGE,"E31.11.0.5"),sQuery(id+"F0.wireOp",EDGE,"E31.12.0.0"),sQuery(id+"F0.wireOp",EDGE,"E31.12.0.1"),sQuery(id+"F0.wireOp",EDGE,"E31.12.0.2"),sQuery(id+"F0.wireOp",EDGE,"E31.12.0.3"),sQuery(id+"F0.wireOp",EDGE,"E31.12.0.4"),sQuery(id+"F0.wireOp",EDGE,"E31.12.0.5"),sQuery(id+"F0.wireOp",EDGE,"E31.13.0.0"),sQuery(id+"F0.wireOp",EDGE,"E31.13.0.1"),sQuery(id+"F0.wireOp",EDGE,"E31.13.0.2"),sQuery(id+"F0.wireOp",EDGE,"E31.13.0.3"),sQuery(id+"F0.wireOp",EDGE,"E31.13.0.4"),sQuery(id+"F0.wireOp",EDGE,"E31.13.0.5"),sQuery(id+"F0.wireOp",EDGE,"E31.14.0.0"),sQuery(id+"F0.wireOp",EDGE,"E31.14.0.1"),sQuery(id+"F0.wireOp",EDGE,"E31.14.0.2"),sQuery(id+"F0.wireOp",EDGE,"E31.14.0.3"),sQuery(id+"F0.wireOp",EDGE,"E31.14.0.4"),sQuery(id+"F0.wireOp",EDGE,"E31.14.0.5"),sQuery(id+"F0.wireOp",EDGE,"E31.15.0.0"),sQuery(id+"F0.wireOp",EDGE,"E31.15.0.1"),sQuery(id+"F0.wireOp",EDGE,"E31.15.0.2"),sQuery(id+"F0.wireOp",EDGE,"E31.15.0.3"),sQuery(id+"F0.wireOp",EDGE,"E31.15.0.4"),sQuery(id+"F0.wireOp",EDGE,"E31.15.0.5"),sQuery(id+"F0.wireOp",EDGE,"E31.16.0.0"),sQuery(id+"F0.wireOp",EDGE,"E31.16.0.1"),sQuery(id+"F0.wireOp",EDGE,"E31.16.0.2"),sQuery(id+"F0.wireOp",EDGE,"E31.16.0.3"),sQuery(id+"F0.wireOp",EDGE,"E31.16.0.4"),sQuery(id+"F0.wireOp",EDGE,"E31.16.0.5"),sQuery(id+"F0.wireOp",EDGE,"E31.17.0.0"),sQuery(id+"F0.wireOp",EDGE,"E31.17.0.1"),sQuery(id+"F0.wireOp",EDGE,"E31.17.0.2"),sQuery(id+"F0.wireOp",EDGE,"E31.17.0.3"),sQuery(id+"F0.wireOp",EDGE,"E31.17.0.4"),sQuery(id+"F0.wireOp",EDGE,"E31.17.0.5"),sQuery(id+"F0.wireOp",EDGE,"E31.18.0.0"),sQuery(id+"F0.wireOp",EDGE,"E31.18.0.1"),sQuery(id+"F0.wireOp",EDGE,"E31.18.0.2"),sQuery(id+"F0.wireOp",EDGE,"E31.18.0.3"),sQuery(id+"F0.wireOp",EDGE,"E31.18.0.4"),sQuery(id+"F0.wireOp",EDGE,"E31.18.0.5"),sQuery(id+"F0.wireOp",EDGE,"E32"),sQuery(id+"F0.wireOp",EDGE,"E33"),sQuery(id+"F0.wireOp",EDGE,"E34"),sQuery(id+"F0.wireOp",EDGE,"E36"),sQuery(id+"F0.wireOp",EDGE,"E37"),sQuery(id+"F0.wireOp",EDGE,"E38"),sQuery(id+"F0.wireOp",EDGE,"E39"),sQuery(id+"F0.wireOp",EDGE,"E40"),sQuery(id+"F0.wireOp",EDGE,"E41"),sQuery(id+"F0.wireOp",EDGE,"E42"),sQuery(id+"F0.wireOp",EDGE,"E43"),sQuery(id+"F0.wireOp",EDGE,"E44"),sQuery(id+"F0.wireOp",EDGE,"E45.bottom"),sQuery(id+"F0.wireOp",EDGE,"E45.top"),sQuery(id+"F0.wireOp",EDGE,"E45.left"),sQuery(id+"F0.wireOp",EDGE,"E45.right"),sQuery(id+"F0.wireOp",EDGE,"E46.bottom"),sQuery(id+"F0.wireOp",EDGE,"E46.top"),sQuery(id+"F0.wireOp",EDGE,"E46.left"),sQuery(id+"F0.wireOp",EDGE,"E46.right"),sQuery(id+"F0.wireOp",EDGE,"E47.bottom"),sQuery(id+"F0.wireOp",EDGE,"E47.top"),sQuery(id+"F0.wireOp",EDGE,"E47.left"),sQuery(id+"F0.wireOp",EDGE,"E47.right"),sQuery(id+"F0.wireOp",EDGE,"E56"),sQuery(id+"F0.wireOp",EDGE,"E57"),sQuery(id+"F0.wireOp",EDGE,"E58"),sQuery(id+"F0.wireOp",EDGE,"E59"),sQuery(id+"F0.wireOp",EDGE,"E60"),sQuery(id+"F0.wireOp",EDGE,"E69"),sQuery(id+"F0.wireOp",EDGE,"E70"),sQuery(id+"F0.wireOp",EDGE,"E71"),sQuery(id+"F0.wireOp",EDGE,"E72"),sQuery(id+"F0.wireOp",EDGE,"E73"),sQuery(id+"F0.wireOp",EDGE,"E79"),sQuery(id+"F0.wireOp",EDGE,"E80"),sQuery(id+"F0.wireOp",EDGE,"E85.bottom"),sQuery(id+"F0.wireOp",EDGE,"E85.top"),sQuery(id+"F0.wireOp",EDGE,"E85.left"),sQuery(id+"F0.wireOp",EDGE,"E85.right"),sQuery(id+"F0.wireOp",EDGE,"E86.bottom"),sQuery(id+"F0.wireOp",EDGE,"E86.top"),sQuery(id+"F0.wireOp",EDGE,"E86.left"),sQuery(id+"F0.wireOp",EDGE,"E86.right"),sQuery(id+"F0.wireOp",EDGE,"E87.bottom"),sQuery(id+"F0.wireOp",EDGE,"E87.top"),sQuery(id+"F0.wireOp",EDGE,"E87.left"),sQuery(id+"F0.wireOp",EDGE,"E87.right"),sQuery(id+"F0.wireOp",EDGE,"E88.bottom"),sQuery(id+"F0.wireOp",EDGE,"E88.top"),sQuery(id+"F0.wireOp",EDGE,"E88.left"),sQuery(id+"F0.wireOp",EDGE,"E88.right"),sQuery(id+"F0.wireOp",EDGE,"E89.bottom"),sQuery(id+"F0.wireOp",EDGE,"E89.top"),sQuery(id+"F0.wireOp",EDGE,"E89.left"),sQuery(id+"F0.wireOp",EDGE,"E89.right"),sQuery(id+"F0.wireOp",EDGE,"E90.bottom"),sQuery(id+"F0.wireOp",EDGE,"E90.top"),sQuery(id+"F0.wireOp",EDGE,"E90.left"),sQuery(id+"F0.wireOp",EDGE,"E90.right"),sQuery(id+"F0.wireOp",EDGE,"E92.bottom"),sQuery(id+"F0.wireOp",EDGE,"E92.top"),sQuery(id+"F0.wireOp",EDGE,"E92.left"),sQuery(id+"F0.wireOp",EDGE,"E92.right"),sQuery(id+"F0.wireOp",EDGE,"E93.bottom"),sQuery(id+"F0.wireOp",EDGE,"E93.top"),sQuery(id+"F0.wireOp",EDGE,"E93.left"),sQuery(id+"F0.wireOp",EDGE,"E93.right")])],"isStart":false});
            var sketch = newSketch(context, id + "F2", { "sketchPlane" : qUnion([Q0])});
            skLineSegment(sketch, "E94.bottom", {"start": v(51.58, 19) * mm, "end": v(57.08, 19) * mm});
            skLineSegment(sketch, "E94.top", {"start": v(51.58, 11) * mm, "end": v(57.08, 11) * mm});
            skLineSegment(sketch, "E94.left", {"start": v(51.58, 19) * mm, "end": v(51.58, 11) * mm});
            skLineSegment(sketch, "E94.right", {"start": v(57.08, 19) * mm, "end": v(57.08, 11) * mm});
            skLineSegment(sketch, "E95.bottom", {"start": v(51.33, 18.92) * mm, "end": v(50.08, 18.92) * mm});
            skLineSegment(sketch, "E95.top", {"start": v(51.33, 18.42) * mm, "end": v(50.08, 18.42) * mm});
            skLineSegment(sketch, "E95.left", {"start": v(51.33, 18.92) * mm, "end": v(51.33, 18.42) * mm});
            skLineSegment(sketch, "E95.right", {"start": v(50.08, 18.92) * mm, "end": v(50.08, 18.42) * mm});
            skLineSegment(sketch, "E96", {"start": v(54.33, 19) * mm, "end": v(54.33, 11) * mm, "construction": true});
            skLineSegment(sketch, "E97", {"start": v(50.08, 18.67) * mm, "end": v(54.33, 18.67) * mm, "construction": true});
            skLineSegment(sketch, "E98.1.0.0", {"start": v(50.08, 18.25) * mm, "end": v(50.08, 17.75) * mm});
            skLineSegment(sketch, "E98.1.0.1", {"start": v(51.33, 18.25) * mm, "end": v(50.08, 18.25) * mm});
            skLineSegment(sketch, "E98.1.0.2", {"start": v(51.33, 18.25) * mm, "end": v(51.33, 17.75) * mm});
            skLineSegment(sketch, "E98.1.0.3", {"start": v(51.33, 17.75) * mm, "end": v(50.08, 17.75) * mm});
            skLineSegment(sketch, "E98.2.0.0", {"start": v(50.08, 17.58) * mm, "end": v(50.08, 17.08) * mm});
            skLineSegment(sketch, "E98.2.0.1", {"start": v(51.33, 17.58) * mm, "end": v(50.08, 17.58) * mm});
            skLineSegment(sketch, "E98.2.0.2", {"start": v(51.33, 17.58) * mm, "end": v(51.33, 17.08) * mm});
            skLineSegment(sketch, "E98.2.0.3", {"start": v(51.33, 17.08) * mm, "end": v(50.08, 17.08) * mm});
            skLineSegment(sketch, "E98.3.0.0", {"start": v(50.08, 16.92) * mm, "end": v(50.08, 16.42) * mm});
            skLineSegment(sketch, "E98.3.0.1", {"start": v(51.33, 16.92) * mm, "end": v(50.08, 16.92) * mm});
            skLineSegment(sketch, "E98.3.0.2", {"start": v(51.33, 16.92) * mm, "end": v(51.33, 16.42) * mm});
            skLineSegment(sketch, "E98.3.0.3", {"start": v(51.33, 16.42) * mm, "end": v(50.08, 16.42) * mm});
            skLineSegment(sketch, "E98.4.0.0", {"start": v(50.08, 16.25) * mm, "end": v(50.08, 15.75) * mm});
            skLineSegment(sketch, "E98.4.0.1", {"start": v(51.33, 16.25) * mm, "end": v(50.08, 16.25) * mm});
            skLineSegment(sketch, "E98.4.0.2", {"start": v(51.33, 16.25) * mm, "end": v(51.33, 15.75) * mm});
            skLineSegment(sketch, "E98.4.0.3", {"start": v(51.33, 15.75) * mm, "end": v(50.08, 15.75) * mm});
            skLineSegment(sketch, "E98.5.0.0", {"start": v(50.08, 15.58) * mm, "end": v(50.08, 15.08) * mm});
            skLineSegment(sketch, "E98.5.0.1", {"start": v(51.33, 15.58) * mm, "end": v(50.08, 15.58) * mm});
            skLineSegment(sketch, "E98.5.0.2", {"start": v(51.33, 15.58) * mm, "end": v(51.33, 15.08) * mm});
            skLineSegment(sketch, "E98.5.0.3", {"start": v(51.33, 15.08) * mm, "end": v(50.08, 15.08) * mm});
            skLineSegment(sketch, "E98.6.0.0", {"start": v(50.08, 14.92) * mm, "end": v(50.08, 14.42) * mm});
            skLineSegment(sketch, "E98.6.0.1", {"start": v(51.33, 14.92) * mm, "end": v(50.08, 14.92) * mm});
            skLineSegment(sketch, "E98.6.0.2", {"start": v(51.33, 14.92) * mm, "end": v(51.33, 14.42) * mm});
            skLineSegment(sketch, "E98.6.0.3", {"start": v(51.33, 14.42) * mm, "end": v(50.08, 14.42) * mm});
            skLineSegment(sketch, "E98.7.0.0", {"start": v(50.08, 14.25) * mm, "end": v(50.08, 13.75) * mm});
            skLineSegment(sketch, "E98.7.0.1", {"start": v(51.33, 14.25) * mm, "end": v(50.08, 14.25) * mm});
            skLineSegment(sketch, "E98.7.0.2", {"start": v(51.33, 14.25) * mm, "end": v(51.33, 13.75) * mm});
            skLineSegment(sketch, "E98.7.0.3", {"start": v(51.33, 13.75) * mm, "end": v(50.08, 13.75) * mm});
            skLineSegment(sketch, "E98.8.0.0", {"start": v(50.08, 13.58) * mm, "end": v(50.08, 13.08) * mm});
            skLineSegment(sketch, "E98.8.0.1", {"start": v(51.33, 13.58) * mm, "end": v(50.08, 13.58) * mm});
            skLineSegment(sketch, "E98.8.0.2", {"start": v(51.33, 13.58) * mm, "end": v(51.33, 13.08) * mm});
            skLineSegment(sketch, "E98.8.0.3", {"start": v(51.33, 13.08) * mm, "end": v(50.08, 13.08) * mm});
            skLineSegment(sketch, "E98.9.0.0", {"start": v(50.08, 12.92) * mm, "end": v(50.08, 12.42) * mm});
            skLineSegment(sketch, "E98.9.0.1", {"start": v(51.33, 12.92) * mm, "end": v(50.08, 12.92) * mm});
            skLineSegment(sketch, "E98.9.0.2", {"start": v(51.33, 12.92) * mm, "end": v(51.33, 12.42) * mm});
            skLineSegment(sketch, "E98.9.0.3", {"start": v(51.33, 12.42) * mm, "end": v(50.08, 12.42) * mm});
            skLineSegment(sketch, "E98.10.0.0", {"start": v(50.08, 12.25) * mm, "end": v(50.08, 11.75) * mm});
            skLineSegment(sketch, "E98.10.0.1", {"start": v(51.33, 12.25) * mm, "end": v(50.08, 12.25) * mm});
            skLineSegment(sketch, "E98.10.0.2", {"start": v(51.33, 12.25) * mm, "end": v(51.33, 11.75) * mm});
            skLineSegment(sketch, "E98.10.0.3", {"start": v(51.33, 11.75) * mm, "end": v(50.08, 11.75) * mm});
            skLineSegment(sketch, "E98.11.0.0", {"start": v(50.08, 11.58) * mm, "end": v(50.08, 11.08) * mm});
            skLineSegment(sketch, "E98.11.0.1", {"start": v(51.33, 11.58) * mm, "end": v(50.08, 11.58) * mm});
            skLineSegment(sketch, "E98.11.0.2", {"start": v(51.33, 11.58) * mm, "end": v(51.33, 11.08) * mm});
            skLineSegment(sketch, "E98.11.0.3", {"start": v(51.33, 11.08) * mm, "end": v(50.08, 11.08) * mm});
            skLineSegment(sketch, "E98.direction1", {"start": v(50.08, 18.42) * mm, "end": v(50.08, 17.75) * mm, "construction": true});
            skLineSegment(sketch, "E99.MirrorCS", {"start": v(58.58, 18.25) * mm, "end": v(58.58, 17.75) * mm});
            skLineSegment(sketch, "E100.MirrorCS", {"start": v(57.33, 12.92) * mm, "end": v(57.33, 12.42) * mm});
            skLineSegment(sketch, "E101.MirrorCS", {"start": v(58.58, 12.25) * mm, "end": v(58.58, 11.75) * mm});
            skLineSegment(sketch, "E102.MirrorCS", {"start": v(57.33, 12.25) * mm, "end": v(57.33, 11.75) * mm});
            skLineSegment(sketch, "E103.MirrorCS", {"start": v(57.33, 17.58) * mm, "end": v(57.33, 17.08) * mm});
            skLineSegment(sketch, "E104.MirrorCS", {"start": v(58.58, 16.92) * mm, "end": v(58.58, 16.42) * mm});
            skLineSegment(sketch, "E105.MirrorCS", {"start": v(58.58, 11.58) * mm, "end": v(58.58, 11.08) * mm});
            skLineSegment(sketch, "E106.MirrorCS", {"start": v(58.58, 18.42) * mm, "end": v(58.58, 17.75) * mm, "construction": true});
            skLineSegment(sketch, "E107.MirrorCS", {"start": v(57.33, 16.92) * mm, "end": v(57.33, 16.42) * mm});
            skLineSegment(sketch, "E108.MirrorCS", {"start": v(57.33, 18.25) * mm, "end": v(57.33, 17.75) * mm});
            skLineSegment(sketch, "E109.MirrorCS", {"start": v(58.58, 18.92) * mm, "end": v(58.58, 18.42) * mm});
            skLineSegment(sketch, "E110.MirrorCS", {"start": v(58.58, 12.92) * mm, "end": v(58.58, 12.42) * mm});
            skLineSegment(sketch, "E111.MirrorCS", {"start": v(58.58, 17.58) * mm, "end": v(58.58, 17.08) * mm});
            skLineSegment(sketch, "E112.MirrorCS", {"start": v(57.33, 11.58) * mm, "end": v(57.33, 11.08) * mm});
            skLineSegment(sketch, "E113.MirrorCS", {"start": v(57.33, 12.92) * mm, "end": v(58.58, 12.92) * mm});
            skLineSegment(sketch, "E114.MirrorCS", {"start": v(57.33, 15.58) * mm, "end": v(58.58, 15.58) * mm});
            skLineSegment(sketch, "E115.MirrorCS", {"start": v(57.33, 15.08) * mm, "end": v(58.58, 15.08) * mm});
            skLineSegment(sketch, "E116.MirrorCS", {"start": v(57.33, 12.42) * mm, "end": v(58.58, 12.42) * mm});
            skLineSegment(sketch, "E117.MirrorCS", {"start": v(57.33, 15.58) * mm, "end": v(57.33, 15.08) * mm});
            skLineSegment(sketch, "E118.MirrorCS", {"start": v(58.58, 14.92) * mm, "end": v(58.58, 14.42) * mm});
            skLineSegment(sketch, "E119.MirrorCS", {"start": v(57.33, 14.92) * mm, "end": v(58.58, 14.92) * mm});
            skLineSegment(sketch, "E120.MirrorCS", {"start": v(57.33, 12.25) * mm, "end": v(58.58, 12.25) * mm});
            skLineSegment(sketch, "E121.MirrorCS", {"start": v(57.33, 14.92) * mm, "end": v(57.33, 14.42) * mm});
            skLineSegment(sketch, "E122.MirrorCS", {"start": v(57.33, 14.42) * mm, "end": v(58.58, 14.42) * mm});
            skLineSegment(sketch, "E123.MirrorCS", {"start": v(57.33, 17.08) * mm, "end": v(58.58, 17.08) * mm});
            skLineSegment(sketch, "E124.MirrorCS", {"start": v(57.33, 11.75) * mm, "end": v(58.58, 11.75) * mm});
            skLineSegment(sketch, "E125.MirrorCS", {"start": v(58.58, 14.25) * mm, "end": v(58.58, 13.75) * mm});
            skLineSegment(sketch, "E126.MirrorCS", {"start": v(57.33, 14.25) * mm, "end": v(58.58, 14.25) * mm});
            skLineSegment(sketch, "E127.MirrorCS", {"start": v(57.33, 16.25) * mm, "end": v(58.58, 16.25) * mm});
            skLineSegment(sketch, "E128.MirrorCS", {"start": v(57.33, 13.58) * mm, "end": v(58.58, 13.58) * mm});
            skLineSegment(sketch, "E129.MirrorCS", {"start": v(57.33, 18.42) * mm, "end": v(58.58, 18.42) * mm});
            skLineSegment(sketch, "E130.MirrorCS", {"start": v(57.33, 18.92) * mm, "end": v(58.58, 18.92) * mm});
            skLineSegment(sketch, "E131.MirrorCS", {"start": v(57.33, 17.58) * mm, "end": v(58.58, 17.58) * mm});
            skLineSegment(sketch, "E132.MirrorCS", {"start": v(57.33, 14.25) * mm, "end": v(57.33, 13.75) * mm});
            skLineSegment(sketch, "E133.MirrorCS", {"start": v(58.58, 15.58) * mm, "end": v(58.58, 15.08) * mm});
            skLineSegment(sketch, "E134.MirrorCS", {"start": v(57.33, 11.08) * mm, "end": v(58.58, 11.08) * mm});
            skLineSegment(sketch, "E135.MirrorCS", {"start": v(57.33, 16.92) * mm, "end": v(58.58, 16.92) * mm});
            skLineSegment(sketch, "E136.MirrorCS", {"start": v(57.33, 17.75) * mm, "end": v(58.58, 17.75) * mm});
            skLineSegment(sketch, "E137.MirrorCS", {"start": v(57.33, 13.08) * mm, "end": v(58.58, 13.08) * mm});
            skLineSegment(sketch, "E138.MirrorCS", {"start": v(57.33, 18.25) * mm, "end": v(58.58, 18.25) * mm});
            skLineSegment(sketch, "E139.MirrorCS", {"start": v(57.33, 15.75) * mm, "end": v(58.58, 15.75) * mm});
            skLineSegment(sketch, "E140.MirrorCS", {"start": v(57.33, 18.92) * mm, "end": v(57.33, 18.42) * mm});
            skLineSegment(sketch, "E141.MirrorCS", {"start": v(57.33, 16.42) * mm, "end": v(58.58, 16.42) * mm});
            skLineSegment(sketch, "E142.MirrorCS", {"start": v(57.33, 13.75) * mm, "end": v(58.58, 13.75) * mm});
            skLineSegment(sketch, "E143.MirrorCS", {"start": v(57.33, 11.58) * mm, "end": v(58.58, 11.58) * mm});
            skLineSegment(sketch, "E144.MirrorCS", {"start": v(57.33, 16.25) * mm, "end": v(57.33, 15.75) * mm});
            skLineSegment(sketch, "E145.MirrorCS", {"start": v(57.33, 13.58) * mm, "end": v(57.33, 13.08) * mm});
            skLineSegment(sketch, "E146.MirrorCS", {"start": v(58.58, 13.58) * mm, "end": v(58.58, 13.08) * mm});
            skLineSegment(sketch, "E147.MirrorCS", {"start": v(58.58, 16.25) * mm, "end": v(58.58, 15.75) * mm});
            skLineSegment(sketch, "E148.bottom", {"start": v(11, 27) * mm, "end": v(16.5, 27) * mm});
            skLineSegment(sketch, "E148.top", {"start": v(11, 19) * mm, "end": v(16.5, 19) * mm});
            skLineSegment(sketch, "E148.left", {"start": v(11, 27) * mm, "end": v(11, 19) * mm});
            skLineSegment(sketch, "E148.right", {"start": v(16.5, 27) * mm, "end": v(16.5, 19) * mm});
            skLineSegment(sketch, "E149", {"start": v(13.75, 27) * mm, "end": v(13.75, 19) * mm, "construction": true});
            skLineSegment(sketch, "E150.bottom", {"start": v(9.5, 26.92) * mm, "end": v(10.75, 26.92) * mm});
            skLineSegment(sketch, "E150.top", {"start": v(9.5, 26.42) * mm, "end": v(10.75, 26.42) * mm});
            skLineSegment(sketch, "E150.left", {"start": v(9.5, 26.92) * mm, "end": v(9.5, 26.42) * mm});
            skLineSegment(sketch, "E150.right", {"start": v(10.75, 26.92) * mm, "end": v(10.75, 26.42) * mm});
            skLineSegment(sketch, "E151", {"start": v(9.5, 26.67) * mm, "end": v(13.75, 26.67) * mm, "construction": true});
            skLineSegment(sketch, "E152.1.0.0", {"start": v(10.75, 26.25) * mm, "end": v(10.75, 25.75) * mm});
            skLineSegment(sketch, "E152.1.0.1", {"start": v(9.5, 26.25) * mm, "end": v(9.5, 25.75) * mm});
            skLineSegment(sketch, "E152.1.0.2", {"start": v(9.5, 25.75) * mm, "end": v(10.75, 25.75) * mm});
            skLineSegment(sketch, "E152.1.0.3", {"start": v(9.5, 26.25) * mm, "end": v(10.75, 26.25) * mm});
            skLineSegment(sketch, "E152.2.0.0", {"start": v(10.75, 25.58) * mm, "end": v(10.75, 25.08) * mm});
            skLineSegment(sketch, "E152.2.0.1", {"start": v(9.5, 25.58) * mm, "end": v(9.5, 25.08) * mm});
            skLineSegment(sketch, "E152.2.0.2", {"start": v(9.5, 25.08) * mm, "end": v(10.75, 25.08) * mm});
            skLineSegment(sketch, "E152.2.0.3", {"start": v(9.5, 25.58) * mm, "end": v(10.75, 25.58) * mm});
            skLineSegment(sketch, "E152.3.0.0", {"start": v(10.75, 24.92) * mm, "end": v(10.75, 24.42) * mm});
            skLineSegment(sketch, "E152.3.0.1", {"start": v(9.5, 24.92) * mm, "end": v(9.5, 24.42) * mm});
            skLineSegment(sketch, "E152.3.0.2", {"start": v(9.5, 24.42) * mm, "end": v(10.75, 24.42) * mm});
            skLineSegment(sketch, "E152.3.0.3", {"start": v(9.5, 24.92) * mm, "end": v(10.75, 24.92) * mm});
            skLineSegment(sketch, "E152.4.0.0", {"start": v(10.75, 24.25) * mm, "end": v(10.75, 23.75) * mm});
            skLineSegment(sketch, "E152.4.0.1", {"start": v(9.5, 24.25) * mm, "end": v(9.5, 23.75) * mm});
            skLineSegment(sketch, "E152.4.0.2", {"start": v(9.5, 23.75) * mm, "end": v(10.75, 23.75) * mm});
            skLineSegment(sketch, "E152.4.0.3", {"start": v(9.5, 24.25) * mm, "end": v(10.75, 24.25) * mm});
            skLineSegment(sketch, "E152.5.0.0", {"start": v(10.75, 23.58) * mm, "end": v(10.75, 23.08) * mm});
            skLineSegment(sketch, "E152.5.0.1", {"start": v(9.5, 23.58) * mm, "end": v(9.5, 23.08) * mm});
            skLineSegment(sketch, "E152.5.0.2", {"start": v(9.5, 23.08) * mm, "end": v(10.75, 23.08) * mm});
            skLineSegment(sketch, "E152.5.0.3", {"start": v(9.5, 23.58) * mm, "end": v(10.75, 23.58) * mm});
            skLineSegment(sketch, "E152.6.0.0", {"start": v(10.75, 22.92) * mm, "end": v(10.75, 22.42) * mm});
            skLineSegment(sketch, "E152.6.0.1", {"start": v(9.5, 22.92) * mm, "end": v(9.5, 22.42) * mm});
            skLineSegment(sketch, "E152.6.0.2", {"start": v(9.5, 22.42) * mm, "end": v(10.75, 22.42) * mm});
            skLineSegment(sketch, "E152.6.0.3", {"start": v(9.5, 22.92) * mm, "end": v(10.75, 22.92) * mm});
            skLineSegment(sketch, "E152.7.0.0", {"start": v(10.75, 22.25) * mm, "end": v(10.75, 21.75) * mm});
            skLineSegment(sketch, "E152.7.0.1", {"start": v(9.5, 22.25) * mm, "end": v(9.5, 21.75) * mm});
            skLineSegment(sketch, "E152.7.0.2", {"start": v(9.5, 21.75) * mm, "end": v(10.75, 21.75) * mm});
            skLineSegment(sketch, "E152.7.0.3", {"start": v(9.5, 22.25) * mm, "end": v(10.75, 22.25) * mm});
            skLineSegment(sketch, "E152.8.0.0", {"start": v(10.75, 21.58) * mm, "end": v(10.75, 21.08) * mm});
            skLineSegment(sketch, "E152.8.0.1", {"start": v(9.5, 21.58) * mm, "end": v(9.5, 21.08) * mm});
            skLineSegment(sketch, "E152.8.0.2", {"start": v(9.5, 21.08) * mm, "end": v(10.75, 21.08) * mm});
            skLineSegment(sketch, "E152.8.0.3", {"start": v(9.5, 21.58) * mm, "end": v(10.75, 21.58) * mm});
            skLineSegment(sketch, "E152.9.0.0", {"start": v(10.75, 20.92) * mm, "end": v(10.75, 20.42) * mm});
            skLineSegment(sketch, "E152.9.0.1", {"start": v(9.5, 20.92) * mm, "end": v(9.5, 20.42) * mm});
            skLineSegment(sketch, "E152.9.0.2", {"start": v(9.5, 20.42) * mm, "end": v(10.75, 20.42) * mm});
            skLineSegment(sketch, "E152.9.0.3", {"start": v(9.5, 20.92) * mm, "end": v(10.75, 20.92) * mm});
            skLineSegment(sketch, "E152.10.0.0", {"start": v(10.75, 20.25) * mm, "end": v(10.75, 19.75) * mm});
            skLineSegment(sketch, "E152.10.0.1", {"start": v(9.5, 20.25) * mm, "end": v(9.5, 19.75) * mm});
            skLineSegment(sketch, "E152.10.0.2", {"start": v(9.5, 19.75) * mm, "end": v(10.75, 19.75) * mm});
            skLineSegment(sketch, "E152.10.0.3", {"start": v(9.5, 20.25) * mm, "end": v(10.75, 20.25) * mm});
            skLineSegment(sketch, "E152.11.0.0", {"start": v(10.75, 19.58) * mm, "end": v(10.75, 19.08) * mm});
            skLineSegment(sketch, "E152.11.0.1", {"start": v(9.5, 19.58) * mm, "end": v(9.5, 19.08) * mm});
            skLineSegment(sketch, "E152.11.0.2", {"start": v(9.5, 19.08) * mm, "end": v(10.75, 19.08) * mm});
            skLineSegment(sketch, "E152.11.0.3", {"start": v(9.5, 19.58) * mm, "end": v(10.75, 19.58) * mm});
            skLineSegment(sketch, "E152.direction1", {"start": v(9.5, 26.42) * mm, "end": v(9.5, 25.75) * mm, "construction": true});
            skLineSegment(sketch, "E153.MirrorCS", {"start": v(18, 26.92) * mm, "end": v(18, 26.42) * mm});
            skLineSegment(sketch, "E154.MirrorCS", {"start": v(18, 26.25) * mm, "end": v(18, 25.75) * mm});
            skLineSegment(sketch, "E155.MirrorCS", {"start": v(18, 21.08) * mm, "end": v(16.75, 21.08) * mm});
            skLineSegment(sketch, "E156.MirrorCS", {"start": v(18, 23.75) * mm, "end": v(16.75, 23.75) * mm});
            skLineSegment(sketch, "E157.MirrorCS", {"start": v(16.75, 26.92) * mm, "end": v(16.75, 26.42) * mm});
            skLineSegment(sketch, "E158.MirrorCS", {"start": v(18, 21.58) * mm, "end": v(18, 21.08) * mm});
            skLineSegment(sketch, "E159.MirrorCS", {"start": v(18, 24.42) * mm, "end": v(16.75, 24.42) * mm});
            skLineSegment(sketch, "E160.MirrorCS", {"start": v(18, 24.25) * mm, "end": v(18, 23.75) * mm});
            skLineSegment(sketch, "E161.MirrorCS", {"start": v(18, 26.92) * mm, "end": v(16.75, 26.92) * mm});
            skLineSegment(sketch, "E162.MirrorCS", {"start": v(18, 26.42) * mm, "end": v(18, 25.75) * mm, "construction": true});
            skLineSegment(sketch, "E163.MirrorCS", {"start": v(16.75, 21.58) * mm, "end": v(16.75, 21.08) * mm});
            skLineSegment(sketch, "E164.MirrorCS", {"start": v(16.75, 24.25) * mm, "end": v(16.75, 23.75) * mm});
            skLineSegment(sketch, "E165.MirrorCS", {"start": v(18, 26.42) * mm, "end": v(16.75, 26.42) * mm});
            skLineSegment(sketch, "E166.MirrorCS", {"start": v(18, 19.58) * mm, "end": v(16.75, 19.58) * mm});
            skLineSegment(sketch, "E167.MirrorCS", {"start": v(18, 24.92) * mm, "end": v(16.75, 24.92) * mm});
            skLineSegment(sketch, "E168.MirrorCS", {"start": v(18, 22.25) * mm, "end": v(16.75, 22.25) * mm});
            skLineSegment(sketch, "E169.MirrorCS", {"start": v(18, 21.75) * mm, "end": v(16.75, 21.75) * mm});
            skLineSegment(sketch, "E170.MirrorCS", {"start": v(18, 19.08) * mm, "end": v(16.75, 19.08) * mm});
            skLineSegment(sketch, "E171.MirrorCS", {"start": v(16.75, 24.92) * mm, "end": v(16.75, 24.42) * mm});
            skLineSegment(sketch, "E172.MirrorCS", {"start": v(16.75, 22.25) * mm, "end": v(16.75, 21.75) * mm});
            skLineSegment(sketch, "E173.MirrorCS", {"start": v(16.75, 19.58) * mm, "end": v(16.75, 19.08) * mm});
            skLineSegment(sketch, "E174.MirrorCS", {"start": v(18, 25.58) * mm, "end": v(16.75, 25.58) * mm});
            skLineSegment(sketch, "E175.MirrorCS", {"start": v(18, 22.92) * mm, "end": v(16.75, 22.92) * mm});
            skLineSegment(sketch, "E176.MirrorCS", {"start": v(18, 20.25) * mm, "end": v(16.75, 20.25) * mm});
            skLineSegment(sketch, "E177.MirrorCS", {"start": v(18, 19.58) * mm, "end": v(18, 19.08) * mm});
            skLineSegment(sketch, "E178.MirrorCS", {"start": v(18, 22.25) * mm, "end": v(18, 21.75) * mm});
            skLineSegment(sketch, "E179.MirrorCS", {"start": v(18, 24.92) * mm, "end": v(18, 24.42) * mm});
            skLineSegment(sketch, "E180.MirrorCS", {"start": v(18, 21.58) * mm, "end": v(16.75, 21.58) * mm});
            skLineSegment(sketch, "E181.MirrorCS", {"start": v(18, 24.25) * mm, "end": v(16.75, 24.25) * mm});
            skLineSegment(sketch, "E182.MirrorCS", {"start": v(16.75, 23.58) * mm, "end": v(16.75, 23.08) * mm});
            skLineSegment(sketch, "E183.MirrorCS", {"start": v(16.75, 26.25) * mm, "end": v(16.75, 25.75) * mm});
            skLineSegment(sketch, "E184.MirrorCS", {"start": v(16.75, 20.92) * mm, "end": v(16.75, 20.42) * mm});
            skLineSegment(sketch, "E185.MirrorCS", {"start": v(18, 23.58) * mm, "end": v(18, 23.08) * mm});
            skLineSegment(sketch, "E186.MirrorCS", {"start": v(18, 20.92) * mm, "end": v(18, 20.42) * mm});
            skLineSegment(sketch, "E187.MirrorCS", {"start": v(18, 23.08) * mm, "end": v(16.75, 23.08) * mm});
            skLineSegment(sketch, "E188.MirrorCS", {"start": v(18, 25.75) * mm, "end": v(16.75, 25.75) * mm});
            skLineSegment(sketch, "E189.MirrorCS", {"start": v(18, 20.42) * mm, "end": v(16.75, 20.42) * mm});
            skLineSegment(sketch, "E190.MirrorCS", {"start": v(16.75, 20.25) * mm, "end": v(16.75, 19.75) * mm});
            skLineSegment(sketch, "E191.MirrorCS", {"start": v(16.75, 22.92) * mm, "end": v(16.75, 22.42) * mm});
            skLineSegment(sketch, "E192.MirrorCS", {"start": v(16.75, 25.58) * mm, "end": v(16.75, 25.08) * mm});
            skLineSegment(sketch, "E193.MirrorCS", {"start": v(18, 25.58) * mm, "end": v(18, 25.08) * mm});
            skLineSegment(sketch, "E194.MirrorCS", {"start": v(18, 22.92) * mm, "end": v(18, 22.42) * mm});
            skLineSegment(sketch, "E195.MirrorCS", {"start": v(18, 20.25) * mm, "end": v(18, 19.75) * mm});
            skLineSegment(sketch, "E196.MirrorCS", {"start": v(18, 26.25) * mm, "end": v(16.75, 26.25) * mm});
            skLineSegment(sketch, "E197.MirrorCS", {"start": v(18, 23.58) * mm, "end": v(16.75, 23.58) * mm});
            skLineSegment(sketch, "E198.MirrorCS", {"start": v(18, 22.42) * mm, "end": v(16.75, 22.42) * mm});
            skLineSegment(sketch, "E199.MirrorCS", {"start": v(18, 19.75) * mm, "end": v(16.75, 19.75) * mm});
            skLineSegment(sketch, "E200.MirrorCS", {"start": v(18, 25.08) * mm, "end": v(16.75, 25.08) * mm});
            skLineSegment(sketch, "E201.MirrorCS", {"start": v(18, 20.92) * mm, "end": v(16.75, 20.92) * mm});
            skLineSegment(sketch, "E202.bottom", {"start": v(32.58, 27.44) * mm, "end": v(36.88, 27.44) * mm});
            skLineSegment(sketch, "E202.top", {"start": v(32.58, 17.64) * mm, "end": v(36.88, 17.64) * mm});
            skLineSegment(sketch, "E202.left", {"start": v(32.58, 27.44) * mm, "end": v(32.58, 17.64) * mm});
            skLineSegment(sketch, "E202.right", {"start": v(36.88, 27.44) * mm, "end": v(36.88, 17.64) * mm});
            skLineSegment(sketch, "E203.bottom", {"start": v(31.08, 27.12) * mm, "end": v(32.33, 27.12) * mm});
            skLineSegment(sketch, "E203.top", {"start": v(31.08, 26.62) * mm, "end": v(32.33, 26.62) * mm});
            skLineSegment(sketch, "E203.left", {"start": v(31.08, 27.12) * mm, "end": v(31.08, 26.62) * mm});
            skLineSegment(sketch, "E203.right", {"start": v(32.33, 27.12) * mm, "end": v(32.33, 26.62) * mm});
            skLineSegment(sketch, "E204", {"start": v(34.73, 27.44) * mm, "end": v(34.73, 17.64) * mm, "construction": true});
            skLineSegment(sketch, "E205", {"start": v(31.08, 26.87) * mm, "end": v(34.73, 26.87) * mm, "construction": true});
            skLineSegment(sketch, "E206.1.0.0", {"start": v(32.33, 26.46) * mm, "end": v(32.33, 25.96) * mm});
            skLineSegment(sketch, "E206.1.0.1", {"start": v(31.08, 26.46) * mm, "end": v(31.08, 25.96) * mm});
            skLineSegment(sketch, "E206.1.0.2", {"start": v(31.08, 25.96) * mm, "end": v(32.33, 25.96) * mm});
            skLineSegment(sketch, "E206.1.0.3", {"start": v(31.08, 26.46) * mm, "end": v(32.33, 26.46) * mm});
            skLineSegment(sketch, "E206.2.0.0", {"start": v(32.33, 25.8) * mm, "end": v(32.33, 25.3) * mm});
            skLineSegment(sketch, "E206.2.0.1", {"start": v(31.08, 25.8) * mm, "end": v(31.08, 25.3) * mm});
            skLineSegment(sketch, "E206.2.0.2", {"start": v(31.08, 25.3) * mm, "end": v(32.33, 25.3) * mm});
            skLineSegment(sketch, "E206.2.0.3", {"start": v(31.08, 25.8) * mm, "end": v(32.33, 25.8) * mm});
            skLineSegment(sketch, "E206.3.0.0", {"start": v(32.33, 25.12) * mm, "end": v(32.33, 24.62) * mm});
            skLineSegment(sketch, "E206.3.0.1", {"start": v(31.08, 25.12) * mm, "end": v(31.08, 24.62) * mm});
            skLineSegment(sketch, "E206.3.0.2", {"start": v(31.08, 24.62) * mm, "end": v(32.33, 24.62) * mm});
            skLineSegment(sketch, "E206.3.0.3", {"start": v(31.08, 25.12) * mm, "end": v(32.33, 25.12) * mm});
            skLineSegment(sketch, "E206.4.0.0", {"start": v(32.33, 24.46) * mm, "end": v(32.33, 23.96) * mm});
            skLineSegment(sketch, "E206.4.0.1", {"start": v(31.08, 24.46) * mm, "end": v(31.08, 23.96) * mm});
            skLineSegment(sketch, "E206.4.0.2", {"start": v(31.08, 23.96) * mm, "end": v(32.33, 23.96) * mm});
            skLineSegment(sketch, "E206.4.0.3", {"start": v(31.08, 24.46) * mm, "end": v(32.33, 24.46) * mm});
            skLineSegment(sketch, "E206.5.0.0", {"start": v(32.33, 23.8) * mm, "end": v(32.33, 23.3) * mm});
            skLineSegment(sketch, "E206.5.0.1", {"start": v(31.08, 23.8) * mm, "end": v(31.08, 23.3) * mm});
            skLineSegment(sketch, "E206.5.0.2", {"start": v(31.08, 23.3) * mm, "end": v(32.33, 23.3) * mm});
            skLineSegment(sketch, "E206.5.0.3", {"start": v(31.08, 23.8) * mm, "end": v(32.33, 23.8) * mm});
            skLineSegment(sketch, "E206.6.0.0", {"start": v(32.33, 23.12) * mm, "end": v(32.33, 22.62) * mm});
            skLineSegment(sketch, "E206.6.0.1", {"start": v(31.08, 23.12) * mm, "end": v(31.08, 22.62) * mm});
            skLineSegment(sketch, "E206.6.0.2", {"start": v(31.08, 22.62) * mm, "end": v(32.33, 22.62) * mm});
            skLineSegment(sketch, "E206.6.0.3", {"start": v(31.08, 23.12) * mm, "end": v(32.33, 23.12) * mm});
            skLineSegment(sketch, "E206.7.0.0", {"start": v(32.33, 22.46) * mm, "end": v(32.33, 21.96) * mm});
            skLineSegment(sketch, "E206.7.0.1", {"start": v(31.08, 22.46) * mm, "end": v(31.08, 21.96) * mm});
            skLineSegment(sketch, "E206.7.0.2", {"start": v(31.08, 21.96) * mm, "end": v(32.33, 21.96) * mm});
            skLineSegment(sketch, "E206.7.0.3", {"start": v(31.08, 22.46) * mm, "end": v(32.33, 22.46) * mm});
            skLineSegment(sketch, "E206.8.0.0", {"start": v(32.33, 21.8) * mm, "end": v(32.33, 21.3) * mm});
            skLineSegment(sketch, "E206.8.0.1", {"start": v(31.08, 21.8) * mm, "end": v(31.08, 21.3) * mm});
            skLineSegment(sketch, "E206.8.0.2", {"start": v(31.08, 21.3) * mm, "end": v(32.33, 21.3) * mm});
            skLineSegment(sketch, "E206.8.0.3", {"start": v(31.08, 21.8) * mm, "end": v(32.33, 21.8) * mm});
            skLineSegment(sketch, "E206.9.0.0", {"start": v(32.33, 21.12) * mm, "end": v(32.33, 20.62) * mm});
            skLineSegment(sketch, "E206.9.0.1", {"start": v(31.08, 21.12) * mm, "end": v(31.08, 20.62) * mm});
            skLineSegment(sketch, "E206.9.0.2", {"start": v(31.08, 20.62) * mm, "end": v(32.33, 20.62) * mm});
            skLineSegment(sketch, "E206.9.0.3", {"start": v(31.08, 21.12) * mm, "end": v(32.33, 21.12) * mm});
            skLineSegment(sketch, "E206.10.0.0", {"start": v(32.33, 20.46) * mm, "end": v(32.33, 19.96) * mm});
            skLineSegment(sketch, "E206.10.0.1", {"start": v(31.08, 20.46) * mm, "end": v(31.08, 19.96) * mm});
            skLineSegment(sketch, "E206.10.0.2", {"start": v(31.08, 19.96) * mm, "end": v(32.33, 19.96) * mm});
            skLineSegment(sketch, "E206.10.0.3", {"start": v(31.08, 20.46) * mm, "end": v(32.33, 20.46) * mm});
            skLineSegment(sketch, "E206.11.0.0", {"start": v(32.33, 19.8) * mm, "end": v(32.33, 19.3) * mm});
            skLineSegment(sketch, "E206.11.0.1", {"start": v(31.08, 19.8) * mm, "end": v(31.08, 19.3) * mm});
            skLineSegment(sketch, "E206.11.0.2", {"start": v(31.08, 19.3) * mm, "end": v(32.33, 19.3) * mm});
            skLineSegment(sketch, "E206.11.0.3", {"start": v(31.08, 19.8) * mm, "end": v(32.33, 19.8) * mm});
            skLineSegment(sketch, "E206.12.0.0", {"start": v(32.33, 19.12) * mm, "end": v(32.33, 18.62) * mm});
            skLineSegment(sketch, "E206.12.0.1", {"start": v(31.08, 19.12) * mm, "end": v(31.08, 18.62) * mm});
            skLineSegment(sketch, "E206.12.0.2", {"start": v(31.08, 18.62) * mm, "end": v(32.33, 18.62) * mm});
            skLineSegment(sketch, "E206.12.0.3", {"start": v(31.08, 19.12) * mm, "end": v(32.33, 19.12) * mm});
            skLineSegment(sketch, "E206.13.0.0", {"start": v(32.33, 18.46) * mm, "end": v(32.33, 17.96) * mm});
            skLineSegment(sketch, "E206.13.0.1", {"start": v(31.08, 18.46) * mm, "end": v(31.08, 17.96) * mm});
            skLineSegment(sketch, "E206.13.0.2", {"start": v(31.08, 17.96) * mm, "end": v(32.33, 17.96) * mm});
            skLineSegment(sketch, "E206.13.0.3", {"start": v(31.08, 18.46) * mm, "end": v(32.33, 18.46) * mm});
            skLineSegment(sketch, "E206.direction1", {"start": v(31.08, 26.62) * mm, "end": v(31.08, 25.96) * mm, "construction": true});
            skLineSegment(sketch, "E207", {"start": v(31.08, 18.2) * mm, "end": v(34.73, 18.2) * mm, "construction": true});
            skLineSegment(sketch, "E208", {"start": v(33.75, 18.2) * mm, "end": v(33.75, 17.64) * mm, "construction": true});
            skLineSegment(sketch, "E209", {"start": v(33.75, 26.87) * mm, "end": v(33.75, 27.44) * mm, "construction": true});
            skLineSegment(sketch, "E210.MirrorCS", {"start": v(38.38, 26.46) * mm, "end": v(38.38, 25.96) * mm});
            skLineSegment(sketch, "E211.MirrorCS", {"start": v(38.38, 18.46) * mm, "end": v(38.38, 17.96) * mm});
            skLineSegment(sketch, "E212.MirrorCS", {"start": v(38.38, 27.12) * mm, "end": v(38.38, 26.62) * mm});
            skLineSegment(sketch, "E213.MirrorCS", {"start": v(37.13, 25.8) * mm, "end": v(37.13, 25.3) * mm});
            skLineSegment(sketch, "E214.MirrorCS", {"start": v(37.13, 23.12) * mm, "end": v(37.13, 22.62) * mm});
            skLineSegment(sketch, "E215.MirrorCS", {"start": v(38.38, 20.62) * mm, "end": v(37.13, 20.62) * mm});
            skLineSegment(sketch, "E216.MirrorCS", {"start": v(38.38, 18.46) * mm, "end": v(37.13, 18.46) * mm});
            skLineSegment(sketch, "E217.MirrorCS", {"start": v(38.38, 20.46) * mm, "end": v(38.38, 19.96) * mm});
            skLineSegment(sketch, "E218.MirrorCS", {"start": v(38.38, 17.96) * mm, "end": v(37.13, 17.96) * mm});
            skLineSegment(sketch, "E219.MirrorCS", {"start": v(38.38, 26.46) * mm, "end": v(37.13, 26.46) * mm});
            skLineSegment(sketch, "E220.MirrorCS", {"start": v(38.38, 23.8) * mm, "end": v(37.13, 23.8) * mm});
            skLineSegment(sketch, "E221.MirrorCS", {"start": v(38.38, 26.62) * mm, "end": v(38.38, 25.96) * mm, "construction": true});
            skLineSegment(sketch, "E222.MirrorCS", {"start": v(38.38, 25.8) * mm, "end": v(38.38, 25.3) * mm});
            skLineSegment(sketch, "E223.MirrorCS", {"start": v(37.13, 20.46) * mm, "end": v(37.13, 19.96) * mm});
            skLineSegment(sketch, "E224.MirrorCS", {"start": v(38.38, 21.12) * mm, "end": v(37.13, 21.12) * mm});
            skLineSegment(sketch, "E225.MirrorCS", {"start": v(38.38, 23.12) * mm, "end": v(38.38, 22.62) * mm});
            skLineSegment(sketch, "E226.MirrorCS", {"start": v(38.38, 19.8) * mm, "end": v(38.38, 19.3) * mm});
            skLineSegment(sketch, "E227.MirrorCS", {"start": v(37.13, 25.12) * mm, "end": v(37.13, 24.62) * mm});
            skLineSegment(sketch, "E228.MirrorCS", {"start": v(38.38, 25.3) * mm, "end": v(37.13, 25.3) * mm});
            skLineSegment(sketch, "E229.MirrorCS", {"start": v(38.38, 23.3) * mm, "end": v(37.13, 23.3) * mm});
            skLineSegment(sketch, "E230.MirrorCS", {"start": v(38.38, 22.46) * mm, "end": v(38.38, 21.96) * mm});
            skLineSegment(sketch, "E231.MirrorCS", {"start": v(37.13, 19.8) * mm, "end": v(37.13, 19.3) * mm});
            skLineSegment(sketch, "E232.MirrorCS", {"start": v(38.38, 25.8) * mm, "end": v(37.13, 25.8) * mm});
            skLineSegment(sketch, "E233.MirrorCS", {"start": v(38.38, 20.46) * mm, "end": v(37.13, 20.46) * mm});
            skLineSegment(sketch, "E234.MirrorCS", {"start": v(38.38, 19.96) * mm, "end": v(37.13, 19.96) * mm});
            skLineSegment(sketch, "E235.MirrorCS", {"start": v(38.38, 22.62) * mm, "end": v(37.13, 22.62) * mm});
            skLineSegment(sketch, "E236.MirrorCS", {"start": v(38.38, 25.96) * mm, "end": v(37.13, 25.96) * mm});
            skLineSegment(sketch, "E237.MirrorCS", {"start": v(38.38, 25.12) * mm, "end": v(38.38, 24.62) * mm});
            skLineSegment(sketch, "E238.MirrorCS", {"start": v(38.38, 23.12) * mm, "end": v(37.13, 23.12) * mm});
            skLineSegment(sketch, "E239.MirrorCS", {"start": v(37.13, 22.46) * mm, "end": v(37.13, 21.96) * mm});
            skLineSegment(sketch, "E240.MirrorCS", {"start": v(37.13, 18.46) * mm, "end": v(37.13, 17.96) * mm});
            skLineSegment(sketch, "E241.MirrorCS", {"start": v(37.13, 21.12) * mm, "end": v(37.13, 20.62) * mm});
            skLineSegment(sketch, "E242.MirrorCS", {"start": v(37.13, 26.46) * mm, "end": v(37.13, 25.96) * mm});
            skLineSegment(sketch, "E243.MirrorCS", {"start": v(37.13, 23.8) * mm, "end": v(37.13, 23.3) * mm});
            skLineSegment(sketch, "E244.MirrorCS", {"start": v(38.38, 21.8) * mm, "end": v(37.13, 21.8) * mm});
            skLineSegment(sketch, "E245.MirrorCS", {"start": v(38.38, 19.12) * mm, "end": v(37.13, 19.12) * mm});
            skLineSegment(sketch, "E246.MirrorCS", {"start": v(38.38, 23.8) * mm, "end": v(38.38, 23.3) * mm});
            skLineSegment(sketch, "E247.MirrorCS", {"start": v(38.38, 21.12) * mm, "end": v(38.38, 20.62) * mm});
            skLineSegment(sketch, "E248.MirrorCS", {"start": v(38.38, 19.3) * mm, "end": v(37.13, 19.3) * mm});
            skLineSegment(sketch, "E249.MirrorCS", {"start": v(38.38, 21.96) * mm, "end": v(37.13, 21.96) * mm});
            skLineSegment(sketch, "E250.MirrorCS", {"start": v(38.38, 24.62) * mm, "end": v(37.13, 24.62) * mm});
            skLineSegment(sketch, "E251.MirrorCS", {"start": v(38.38, 27.12) * mm, "end": v(37.13, 27.12) * mm});
            skLineSegment(sketch, "E252.MirrorCS", {"start": v(38.38, 19.8) * mm, "end": v(37.13, 19.8) * mm});
            skLineSegment(sketch, "E253.MirrorCS", {"start": v(38.38, 22.46) * mm, "end": v(37.13, 22.46) * mm});
            skLineSegment(sketch, "E254.MirrorCS", {"start": v(38.38, 26.62) * mm, "end": v(37.13, 26.62) * mm});
            skLineSegment(sketch, "E255.MirrorCS", {"start": v(38.38, 25.12) * mm, "end": v(37.13, 25.12) * mm});
            skLineSegment(sketch, "E256.MirrorCS", {"start": v(37.13, 24.46) * mm, "end": v(37.13, 23.96) * mm});
            skLineSegment(sketch, "E257.MirrorCS", {"start": v(37.13, 19.12) * mm, "end": v(37.13, 18.62) * mm});
            skLineSegment(sketch, "E258.MirrorCS", {"start": v(37.13, 21.8) * mm, "end": v(37.13, 21.3) * mm});
            skLineSegment(sketch, "E259.MirrorCS", {"start": v(38.38, 21.3) * mm, "end": v(37.13, 21.3) * mm});
            skLineSegment(sketch, "E260.MirrorCS", {"start": v(38.38, 18.62) * mm, "end": v(37.13, 18.62) * mm});
            skLineSegment(sketch, "E261.MirrorCS", {"start": v(38.38, 23.96) * mm, "end": v(37.13, 23.96) * mm});
            skLineSegment(sketch, "E262.MirrorCS", {"start": v(38.38, 19.12) * mm, "end": v(38.38, 18.62) * mm});
            skLineSegment(sketch, "E263.MirrorCS", {"start": v(38.38, 21.8) * mm, "end": v(38.38, 21.3) * mm});
            skLineSegment(sketch, "E264.MirrorCS", {"start": v(38.38, 24.46) * mm, "end": v(38.38, 23.96) * mm});
            skLineSegment(sketch, "E265.MirrorCS", {"start": v(37.13, 27.12) * mm, "end": v(37.13, 26.62) * mm});
            skLineSegment(sketch, "E266.MirrorCS", {"start": v(38.38, 24.46) * mm, "end": v(37.13, 24.46) * mm});
            skSolve(sketch);
        }
        {
            var Q0;
            Q0=qSketchRegion(id+"F2",true);
            extrude(context, id + "F3", {"entities" : qUnion([Q0]), "operationType" : NewBodyOperationType.REMOVE, "oppositeDirection" : true, "depth" : 0.25 * mm});
        }
        {
            var Q0;
            Q0=makeQuery(id+"F1.opExtrude","CAP_FACE",FACE,{"disambiguationData":[OSD([sQuery(id+"F0.wireOp",EDGE,"E0.bottom"),sQuery(id+"F0.wireOp",EDGE,"E0.top"),sQuery(id+"F0.wireOp",EDGE,"E0.left"),sQuery(id+"F0.wireOp",EDGE,"E0.right"),sQuery(id+"F0.wireOp",EDGE,"E1"),sQuery(id+"F0.wireOp",EDGE,"E2"),sQuery(id+"F0.wireOp",EDGE,"E3"),sQuery(id+"F0.wireOp",EDGE,"E4.trimOffspring"),sQuery(id+"F0.wireOp",EDGE,"E5"),sQuery(id+"F0.wireOp",EDGE,"E6"),sQuery(id+"F0.wireOp",EDGE,"E7"),sQuery(id+"F0.wireOp",EDGE,"E9"),sQuery(id+"F0.wireOp",EDGE,"E10.1.0.0"),sQuery(id+"F0.wireOp",EDGE,"E10.2.0.0"),sQuery(id+"F0.wireOp",EDGE,"E10.3.0.0"),sQuery(id+"F0.wireOp",EDGE,"E10.4.0.0"),sQuery(id+"F0.wireOp",EDGE,"E10.5.0.0"),sQuery(id+"F0.wireOp",EDGE,"E10.6.0.0"),sQuery(id+"F0.wireOp",EDGE,"E10.7.0.0"),sQuery(id+"F0.wireOp",EDGE,"E11"),sQuery(id+"F0.wireOp",EDGE,"E12.1.0.0"),sQuery(id+"F0.wireOp",EDGE,"E12.2.0.0"),sQuery(id+"F0.wireOp",EDGE,"E12.3.0.0"),sQuery(id+"F0.wireOp",EDGE,"E12.4.0.0"),sQuery(id+"F0.wireOp",EDGE,"E12.5.0.0"),sQuery(id+"F0.wireOp",EDGE,"E12.6.0.0"),sQuery(id+"F0.wireOp",EDGE,"E12.7.0.0"),sQuery(id+"F0.wireOp",EDGE,"E12.8.0.0"),sQuery(id+"F0.wireOp",EDGE,"E12.9.0.0"),sQuery(id+"F0.wireOp",EDGE,"E14"),sQuery(id+"F0.wireOp",EDGE,"E15.1.0.0"),sQuery(id+"F0.wireOp",EDGE,"E15.2.0.0"),sQuery(id+"F0.wireOp",EDGE,"E15.3.0.0"),sQuery(id+"F0.wireOp",EDGE,"E15.4.0.0"),sQuery(id+"F0.wireOp",EDGE,"E15.5.0.0"),sQuery(id+"F0.wireOp",EDGE,"E16"),sQuery(id+"F0.wireOp",EDGE,"E17.1.0.0"),sQuery(id+"F0.wireOp",EDGE,"E17.2.0.0"),sQuery(id+"F0.wireOp",EDGE,"E17.3.0.0"),sQuery(id+"F0.wireOp",EDGE,"E17.4.0.0"),sQuery(id+"F0.wireOp",EDGE,"E17.5.0.0"),sQuery(id+"F0.wireOp",EDGE,"E17.6.0.0"),sQuery(id+"F0.wireOp",EDGE,"E17.7.0.0"),sQuery(id+"F0.wireOp",EDGE,"E19.1.0.2"),sQuery(id+"F0.wireOp",EDGE,"E19.1.0.3"),sQuery(id+"F0.wireOp",EDGE,"E19.1.0.4"),sQuery(id+"F0.wireOp",EDGE,"E19.1.0.6"),sQuery(id+"F0.wireOp",EDGE,"E19.1.0.7"),sQuery(id+"F0.wireOp",EDGE,"E19.1.0.8"),sQuery(id+"F0.wireOp",EDGE,"E19.1.0.9"),sQuery(id+"F0.wireOp",EDGE,"E19.1.0.10"),sQuery(id+"F0.wireOp",EDGE,"E19.1.0.11"),sQuery(id+"F0.wireOp",EDGE,"E19.1.0.12"),sQuery(id+"F0.wireOp",EDGE,"E19.1.0.13"),sQuery(id+"F0.wireOp",EDGE,"E19.1.0.14"),sQuery(id+"F0.wireOp",EDGE,"E19.1.0.15"),sQuery(id+"F0.wireOp",EDGE,"E19.1.0.16"),sQuery(id+"F0.wireOp",EDGE,"E19.1.0.17"),sQuery(id+"F0.wireOp",EDGE,"E19.1.0.18"),sQuery(id+"F0.wireOp",EDGE,"E19.1.0.19"),sQuery(id+"F0.wireOp",EDGE,"E21.1.0.1"),sQuery(id+"F0.wireOp",EDGE,"E21.1.0.2"),sQuery(id+"F0.wireOp",EDGE,"E21.1.0.3"),sQuery(id+"F0.wireOp",EDGE,"E21.1.0.4"),sQuery(id+"F0.wireOp",EDGE,"E21.1.0.5"),sQuery(id+"F0.wireOp",EDGE,"E21.1.0.6"),sQuery(id+"F0.wireOp",EDGE,"E21.1.0.7"),sQuery(id+"F0.wireOp",EDGE,"E21.1.0.8"),sQuery(id+"F0.wireOp",EDGE,"E21.1.0.9"),sQuery(id+"F0.wireOp",EDGE,"E21.1.0.10"),sQuery(id+"F0.wireOp",EDGE,"E21.1.0.11"),sQuery(id+"F0.wireOp",EDGE,"E21.1.0.12"),sQuery(id+"F0.wireOp",EDGE,"E25"),sQuery(id+"F0.wireOp",EDGE,"E26"),sQuery(id+"F0.wireOp",EDGE,"E27"),sQuery(id+"F0.wireOp",EDGE,"E28"),sQuery(id+"F0.wireOp",EDGE,"E29"),sQuery(id+"F0.wireOp",EDGE,"E30"),sQuery(id+"F0.wireOp",EDGE,"E31.1.0.0"),sQuery(id+"F0.wireOp",EDGE,"E31.1.0.1"),sQuery(id+"F0.wireOp",EDGE,"E31.1.0.2"),sQuery(id+"F0.wireOp",EDGE,"E31.1.0.3"),sQuery(id+"F0.wireOp",EDGE,"E31.1.0.4"),sQuery(id+"F0.wireOp",EDGE,"E31.1.0.5"),sQuery(id+"F0.wireOp",EDGE,"E31.2.0.0"),sQuery(id+"F0.wireOp",EDGE,"E31.2.0.1"),sQuery(id+"F0.wireOp",EDGE,"E31.2.0.2"),sQuery(id+"F0.wireOp",EDGE,"E31.2.0.3"),sQuery(id+"F0.wireOp",EDGE,"E31.2.0.4"),sQuery(id+"F0.wireOp",EDGE,"E31.2.0.5"),sQuery(id+"F0.wireOp",EDGE,"E31.3.0.0"),sQuery(id+"F0.wireOp",EDGE,"E31.3.0.1"),sQuery(id+"F0.wireOp",EDGE,"E31.3.0.2"),sQuery(id+"F0.wireOp",EDGE,"E31.3.0.3"),sQuery(id+"F0.wireOp",EDGE,"E31.3.0.4"),sQuery(id+"F0.wireOp",EDGE,"E31.3.0.5"),sQuery(id+"F0.wireOp",EDGE,"E31.4.0.0"),sQuery(id+"F0.wireOp",EDGE,"E31.4.0.1"),sQuery(id+"F0.wireOp",EDGE,"E31.4.0.2"),sQuery(id+"F0.wireOp",EDGE,"E31.4.0.3"),sQuery(id+"F0.wireOp",EDGE,"E31.4.0.4"),sQuery(id+"F0.wireOp",EDGE,"E31.4.0.5"),sQuery(id+"F0.wireOp",EDGE,"E31.5.0.0"),sQuery(id+"F0.wireOp",EDGE,"E31.5.0.1"),sQuery(id+"F0.wireOp",EDGE,"E31.5.0.2"),sQuery(id+"F0.wireOp",EDGE,"E31.5.0.3"),sQuery(id+"F0.wireOp",EDGE,"E31.5.0.4"),sQuery(id+"F0.wireOp",EDGE,"E31.5.0.5"),sQuery(id+"F0.wireOp",EDGE,"E31.6.0.0"),sQuery(id+"F0.wireOp",EDGE,"E31.6.0.1"),sQuery(id+"F0.wireOp",EDGE,"E31.6.0.2"),sQuery(id+"F0.wireOp",EDGE,"E31.6.0.3"),sQuery(id+"F0.wireOp",EDGE,"E31.6.0.4"),sQuery(id+"F0.wireOp",EDGE,"E31.6.0.5"),sQuery(id+"F0.wireOp",EDGE,"E31.7.0.0"),sQuery(id+"F0.wireOp",EDGE,"E31.7.0.1"),sQuery(id+"F0.wireOp",EDGE,"E31.7.0.2"),sQuery(id+"F0.wireOp",EDGE,"E31.7.0.3"),sQuery(id+"F0.wireOp",EDGE,"E31.7.0.4"),sQuery(id+"F0.wireOp",EDGE,"E31.7.0.5"),sQuery(id+"F0.wireOp",EDGE,"E31.8.0.0"),sQuery(id+"F0.wireOp",EDGE,"E31.8.0.1"),sQuery(id+"F0.wireOp",EDGE,"E31.8.0.2"),sQuery(id+"F0.wireOp",EDGE,"E31.8.0.3"),sQuery(id+"F0.wireOp",EDGE,"E31.8.0.4"),sQuery(id+"F0.wireOp",EDGE,"E31.8.0.5"),sQuery(id+"F0.wireOp",EDGE,"E31.9.0.0"),sQuery(id+"F0.wireOp",EDGE,"E31.9.0.1"),sQuery(id+"F0.wireOp",EDGE,"E31.9.0.2"),sQuery(id+"F0.wireOp",EDGE,"E31.9.0.3"),sQuery(id+"F0.wireOp",EDGE,"E31.9.0.4"),sQuery(id+"F0.wireOp",EDGE,"E31.9.0.5"),sQuery(id+"F0.wireOp",EDGE,"E31.10.0.0"),sQuery(id+"F0.wireOp",EDGE,"E31.10.0.1"),sQuery(id+"F0.wireOp",EDGE,"E31.10.0.2"),sQuery(id+"F0.wireOp",EDGE,"E31.10.0.3"),sQuery(id+"F0.wireOp",EDGE,"E31.10.0.4"),sQuery(id+"F0.wireOp",EDGE,"E31.10.0.5"),sQuery(id+"F0.wireOp",EDGE,"E31.11.0.0"),sQuery(id+"F0.wireOp",EDGE,"E31.11.0.1"),sQuery(id+"F0.wireOp",EDGE,"E31.11.0.2"),sQuery(id+"F0.wireOp",EDGE,"E31.11.0.3"),sQuery(id+"F0.wireOp",EDGE,"E31.11.0.4"),sQuery(id+"F0.wireOp",EDGE,"E31.11.0.5"),sQuery(id+"F0.wireOp",EDGE,"E31.12.0.0"),sQuery(id+"F0.wireOp",EDGE,"E31.12.0.1"),sQuery(id+"F0.wireOp",EDGE,"E31.12.0.2"),sQuery(id+"F0.wireOp",EDGE,"E31.12.0.3"),sQuery(id+"F0.wireOp",EDGE,"E31.12.0.4"),sQuery(id+"F0.wireOp",EDGE,"E31.12.0.5"),sQuery(id+"F0.wireOp",EDGE,"E31.13.0.0"),sQuery(id+"F0.wireOp",EDGE,"E31.13.0.1"),sQuery(id+"F0.wireOp",EDGE,"E31.13.0.2"),sQuery(id+"F0.wireOp",EDGE,"E31.13.0.3"),sQuery(id+"F0.wireOp",EDGE,"E31.13.0.4"),sQuery(id+"F0.wireOp",EDGE,"E31.13.0.5"),sQuery(id+"F0.wireOp",EDGE,"E31.14.0.0"),sQuery(id+"F0.wireOp",EDGE,"E31.14.0.1"),sQuery(id+"F0.wireOp",EDGE,"E31.14.0.2"),sQuery(id+"F0.wireOp",EDGE,"E31.14.0.3"),sQuery(id+"F0.wireOp",EDGE,"E31.14.0.4"),sQuery(id+"F0.wireOp",EDGE,"E31.14.0.5"),sQuery(id+"F0.wireOp",EDGE,"E31.15.0.0"),sQuery(id+"F0.wireOp",EDGE,"E31.15.0.1"),sQuery(id+"F0.wireOp",EDGE,"E31.15.0.2"),sQuery(id+"F0.wireOp",EDGE,"E31.15.0.3"),sQuery(id+"F0.wireOp",EDGE,"E31.15.0.4"),sQuery(id+"F0.wireOp",EDGE,"E31.15.0.5"),sQuery(id+"F0.wireOp",EDGE,"E31.16.0.0"),sQuery(id+"F0.wireOp",EDGE,"E31.16.0.1"),sQuery(id+"F0.wireOp",EDGE,"E31.16.0.2"),sQuery(id+"F0.wireOp",EDGE,"E31.16.0.3"),sQuery(id+"F0.wireOp",EDGE,"E31.16.0.4"),sQuery(id+"F0.wireOp",EDGE,"E31.16.0.5"),sQuery(id+"F0.wireOp",EDGE,"E31.17.0.0"),sQuery(id+"F0.wireOp",EDGE,"E31.17.0.1"),sQuery(id+"F0.wireOp",EDGE,"E31.17.0.2"),sQuery(id+"F0.wireOp",EDGE,"E31.17.0.3"),sQuery(id+"F0.wireOp",EDGE,"E31.17.0.4"),sQuery(id+"F0.wireOp",EDGE,"E31.17.0.5"),sQuery(id+"F0.wireOp",EDGE,"E31.18.0.0"),sQuery(id+"F0.wireOp",EDGE,"E31.18.0.1"),sQuery(id+"F0.wireOp",EDGE,"E31.18.0.2"),sQuery(id+"F0.wireOp",EDGE,"E31.18.0.3"),sQuery(id+"F0.wireOp",EDGE,"E31.18.0.4"),sQuery(id+"F0.wireOp",EDGE,"E31.18.0.5"),sQuery(id+"F0.wireOp",EDGE,"E32"),sQuery(id+"F0.wireOp",EDGE,"E33"),sQuery(id+"F0.wireOp",EDGE,"E34"),sQuery(id+"F0.wireOp",EDGE,"E36"),sQuery(id+"F0.wireOp",EDGE,"E37"),sQuery(id+"F0.wireOp",EDGE,"E38"),sQuery(id+"F0.wireOp",EDGE,"E39"),sQuery(id+"F0.wireOp",EDGE,"E40"),sQuery(id+"F0.wireOp",EDGE,"E41"),sQuery(id+"F0.wireOp",EDGE,"E42"),sQuery(id+"F0.wireOp",EDGE,"E43"),sQuery(id+"F0.wireOp",EDGE,"E44"),sQuery(id+"F0.wireOp",EDGE,"E45.bottom"),sQuery(id+"F0.wireOp",EDGE,"E45.top"),sQuery(id+"F0.wireOp",EDGE,"E45.left"),sQuery(id+"F0.wireOp",EDGE,"E45.right"),sQuery(id+"F0.wireOp",EDGE,"E46.bottom"),sQuery(id+"F0.wireOp",EDGE,"E46.top"),sQuery(id+"F0.wireOp",EDGE,"E46.left"),sQuery(id+"F0.wireOp",EDGE,"E46.right"),sQuery(id+"F0.wireOp",EDGE,"E47.bottom"),sQuery(id+"F0.wireOp",EDGE,"E47.top"),sQuery(id+"F0.wireOp",EDGE,"E47.left"),sQuery(id+"F0.wireOp",EDGE,"E47.right"),sQuery(id+"F0.wireOp",EDGE,"E56"),sQuery(id+"F0.wireOp",EDGE,"E57"),sQuery(id+"F0.wireOp",EDGE,"E58"),sQuery(id+"F0.wireOp",EDGE,"E59"),sQuery(id+"F0.wireOp",EDGE,"E60"),sQuery(id+"F0.wireOp",EDGE,"E69"),sQuery(id+"F0.wireOp",EDGE,"E70"),sQuery(id+"F0.wireOp",EDGE,"E71"),sQuery(id+"F0.wireOp",EDGE,"E72"),sQuery(id+"F0.wireOp",EDGE,"E73"),sQuery(id+"F0.wireOp",EDGE,"E79"),sQuery(id+"F0.wireOp",EDGE,"E80"),sQuery(id+"F0.wireOp",EDGE,"E85.bottom"),sQuery(id+"F0.wireOp",EDGE,"E85.top"),sQuery(id+"F0.wireOp",EDGE,"E85.left"),sQuery(id+"F0.wireOp",EDGE,"E85.right"),sQuery(id+"F0.wireOp",EDGE,"E86.bottom"),sQuery(id+"F0.wireOp",EDGE,"E86.top"),sQuery(id+"F0.wireOp",EDGE,"E86.left"),sQuery(id+"F0.wireOp",EDGE,"E86.right"),sQuery(id+"F0.wireOp",EDGE,"E87.bottom"),sQuery(id+"F0.wireOp",EDGE,"E87.top"),sQuery(id+"F0.wireOp",EDGE,"E87.left"),sQuery(id+"F0.wireOp",EDGE,"E87.right"),sQuery(id+"F0.wireOp",EDGE,"E88.bottom"),sQuery(id+"F0.wireOp",EDGE,"E88.top"),sQuery(id+"F0.wireOp",EDGE,"E88.left"),sQuery(id+"F0.wireOp",EDGE,"E88.right"),sQuery(id+"F0.wireOp",EDGE,"E89.bottom"),sQuery(id+"F0.wireOp",EDGE,"E89.top"),sQuery(id+"F0.wireOp",EDGE,"E89.left"),sQuery(id+"F0.wireOp",EDGE,"E89.right"),sQuery(id+"F0.wireOp",EDGE,"E90.bottom"),sQuery(id+"F0.wireOp",EDGE,"E90.top"),sQuery(id+"F0.wireOp",EDGE,"E90.left"),sQuery(id+"F0.wireOp",EDGE,"E90.right"),sQuery(id+"F0.wireOp",EDGE,"E92.bottom"),sQuery(id+"F0.wireOp",EDGE,"E92.top"),sQuery(id+"F0.wireOp",EDGE,"E92.left"),sQuery(id+"F0.wireOp",EDGE,"E92.right"),sQuery(id+"F0.wireOp",EDGE,"E93.bottom"),sQuery(id+"F0.wireOp",EDGE,"E93.top"),sQuery(id+"F0.wireOp",EDGE,"E93.left"),sQuery(id+"F0.wireOp",EDGE,"E93.right")])],"isStart":false});
            var sketch = newSketch(context, id + "F4", { "sketchPlane" : qUnion([Q0])});
            skLineSegment(sketch, "E267.bottom", {"start": v(45.78, 24.4) * mm, "end": v(49.88, 24.4) * mm, "construction": true});
            skLineSegment(sketch, "E267.top", {"start": v(45.78, 19.1) * mm, "end": v(49.88, 19.1) * mm, "construction": true});
            skLineSegment(sketch, "E267.left", {"start": v(45.78, 24.4) * mm, "end": v(45.78, 19.1) * mm, "construction": true});
            skLineSegment(sketch, "E267.right", {"start": v(51.08, 23.2) * mm, "end": v(51.08, 20.3) * mm, "construction": true});
            skLineSegment(sketch, "E268.bottom", {"start": v(11.2, 18) * mm, "end": v(15.3, 18) * mm, "construction": true});
            skLineSegment(sketch, "E268.top", {"start": v(11.2, 12.7) * mm, "end": v(15.3, 12.7) * mm, "construction": true});
            skLineSegment(sketch, "E268.left", {"start": v(11.2, 18) * mm, "end": v(11.2, 12.7) * mm, "construction": true});
            skLineSegment(sketch, "E268.right", {"start": v(16.5, 16.8) * mm, "end": v(16.5, 13.9) * mm, "construction": true});
            skLineSegment(sketch, "E269.bottom", {"start": v(5.9, 44.64) * mm, "end": v(10, 44.64) * mm, "construction": true});
            skLineSegment(sketch, "E269.top", {"start": v(5.9, 39.34) * mm, "end": v(10, 39.34) * mm, "construction": true});
            skLineSegment(sketch, "E269.left", {"start": v(4.7, 43.44) * mm, "end": v(4.7, 40.54) * mm, "construction": true});
            skLineSegment(sketch, "E269.right", {"start": v(10, 44.64) * mm, "end": v(10, 39.34) * mm, "construction": true});
            skLineSegment(sketch, "E270", {"start": v(4.7, 43.44) * mm, "end": v(5.9, 44.64) * mm, "construction": true});
            skLineSegment(sketch, "E271", {"start": v(4.7, 40.54) * mm, "end": v(5.9, 39.34) * mm, "construction": true});
            skPoint(sketch, "E272.orphan", {"position": v(4.7, 44.64) * mm});
            skPoint(sketch, "E273.orphan", {"position": v(4.7, 39.34) * mm});
            skLineSegment(sketch, "E274", {"start": v(15.3, 18) * mm, "end": v(16.5, 16.8) * mm, "construction": true});
            skLineSegment(sketch, "E275", {"start": v(16.5, 13.9) * mm, "end": v(15.3, 12.7) * mm, "construction": true});
            skPoint(sketch, "E276.orphan", {"position": v(16.5, 18) * mm});
            skPoint(sketch, "E277.orphan", {"position": v(16.5, 12.7) * mm});
            skLineSegment(sketch, "E278", {"start": v(51.08, 20.3) * mm, "end": v(49.88, 19.1) * mm, "construction": true});
            skLineSegment(sketch, "E279", {"start": v(49.88, 24.4) * mm, "end": v(51.08, 23.2) * mm, "construction": true});
            skPoint(sketch, "E280.orphan", {"position": v(51.08, 24.4) * mm});
            skPoint(sketch, "E281.orphan", {"position": v(51.08, 19.1) * mm});
            skCircle(sketch, "E282", {"center": v(46.43, 21.75) * mm, "radius": 0.3 * mm});
            skCircle(sketch, "E283", {"center": v(50.43, 21.75) * mm, "radius": 0.3 * mm});
            skLineSegment(sketch, "E284", {"start": v(45.78, 21.75) * mm, "end": v(51.08, 21.75) * mm, "construction": true});
            skLineSegment(sketch, "E285", {"start": v(11.2, 15.35) * mm, "end": v(16.5, 15.35) * mm, "construction": true});
            skCircle(sketch, "E286", {"center": v(11.85, 15.35) * mm, "radius": 0.3 * mm});
            skCircle(sketch, "E287", {"center": v(15.85, 15.35) * mm, "radius": 0.3 * mm});
            skLineSegment(sketch, "E288", {"start": v(4.7, 42) * mm, "end": v(10, 42) * mm, "construction": true});
            skCircle(sketch, "E289", {"center": v(5.35, 42) * mm, "radius": 0.3 * mm});
            skCircle(sketch, "E290", {"center": v(9.35, 42) * mm, "radius": 0.3 * mm});
            skSolve(sketch);
        }
        {
            var Q0;
            Q0=qSketchRegion(id+"F4",true);
            extrude(context, id + "F5", {"entities" : qUnion([Q0]), "operationType" : NewBodyOperationType.REMOVE, "oppositeDirection" : true, "depth" : 0.5 * mm});
        }
        {
            var Q0;
            Q0=makeQuery(id+"F1.opExtrude","CAP_FACE",FACE,{"disambiguationData":[OSD([sQuery(id+"F0.wireOp",EDGE,"E0.bottom"),sQuery(id+"F0.wireOp",EDGE,"E0.top"),sQuery(id+"F0.wireOp",EDGE,"E0.left"),sQuery(id+"F0.wireOp",EDGE,"E0.right"),sQuery(id+"F0.wireOp",EDGE,"E1"),sQuery(id+"F0.wireOp",EDGE,"E2"),sQuery(id+"F0.wireOp",EDGE,"E3"),sQuery(id+"F0.wireOp",EDGE,"E4.trimOffspring"),sQuery(id+"F0.wireOp",EDGE,"E5"),sQuery(id+"F0.wireOp",EDGE,"E6"),sQuery(id+"F0.wireOp",EDGE,"E7"),sQuery(id+"F0.wireOp",EDGE,"E9"),sQuery(id+"F0.wireOp",EDGE,"E10.1.0.0"),sQuery(id+"F0.wireOp",EDGE,"E10.2.0.0"),sQuery(id+"F0.wireOp",EDGE,"E10.3.0.0"),sQuery(id+"F0.wireOp",EDGE,"E10.4.0.0"),sQuery(id+"F0.wireOp",EDGE,"E10.5.0.0"),sQuery(id+"F0.wireOp",EDGE,"E10.6.0.0"),sQuery(id+"F0.wireOp",EDGE,"E10.7.0.0"),sQuery(id+"F0.wireOp",EDGE,"E11"),sQuery(id+"F0.wireOp",EDGE,"E12.1.0.0"),sQuery(id+"F0.wireOp",EDGE,"E12.2.0.0"),sQuery(id+"F0.wireOp",EDGE,"E12.3.0.0"),sQuery(id+"F0.wireOp",EDGE,"E12.4.0.0"),sQuery(id+"F0.wireOp",EDGE,"E12.5.0.0"),sQuery(id+"F0.wireOp",EDGE,"E12.6.0.0"),sQuery(id+"F0.wireOp",EDGE,"E12.7.0.0"),sQuery(id+"F0.wireOp",EDGE,"E12.8.0.0"),sQuery(id+"F0.wireOp",EDGE,"E12.9.0.0"),sQuery(id+"F0.wireOp",EDGE,"E14"),sQuery(id+"F0.wireOp",EDGE,"E15.1.0.0"),sQuery(id+"F0.wireOp",EDGE,"E15.2.0.0"),sQuery(id+"F0.wireOp",EDGE,"E15.3.0.0"),sQuery(id+"F0.wireOp",EDGE,"E15.4.0.0"),sQuery(id+"F0.wireOp",EDGE,"E15.5.0.0"),sQuery(id+"F0.wireOp",EDGE,"E16"),sQuery(id+"F0.wireOp",EDGE,"E17.1.0.0"),sQuery(id+"F0.wireOp",EDGE,"E17.2.0.0"),sQuery(id+"F0.wireOp",EDGE,"E17.3.0.0"),sQuery(id+"F0.wireOp",EDGE,"E17.4.0.0"),sQuery(id+"F0.wireOp",EDGE,"E17.5.0.0"),sQuery(id+"F0.wireOp",EDGE,"E17.6.0.0"),sQuery(id+"F0.wireOp",EDGE,"E17.7.0.0"),sQuery(id+"F0.wireOp",EDGE,"E19.1.0.2"),sQuery(id+"F0.wireOp",EDGE,"E19.1.0.3"),sQuery(id+"F0.wireOp",EDGE,"E19.1.0.4"),sQuery(id+"F0.wireOp",EDGE,"E19.1.0.6"),sQuery(id+"F0.wireOp",EDGE,"E19.1.0.7"),sQuery(id+"F0.wireOp",EDGE,"E19.1.0.8"),sQuery(id+"F0.wireOp",EDGE,"E19.1.0.9"),sQuery(id+"F0.wireOp",EDGE,"E19.1.0.10"),sQuery(id+"F0.wireOp",EDGE,"E19.1.0.11"),sQuery(id+"F0.wireOp",EDGE,"E19.1.0.12"),sQuery(id+"F0.wireOp",EDGE,"E19.1.0.13"),sQuery(id+"F0.wireOp",EDGE,"E19.1.0.14"),sQuery(id+"F0.wireOp",EDGE,"E19.1.0.15"),sQuery(id+"F0.wireOp",EDGE,"E19.1.0.16"),sQuery(id+"F0.wireOp",EDGE,"E19.1.0.17"),sQuery(id+"F0.wireOp",EDGE,"E19.1.0.18"),sQuery(id+"F0.wireOp",EDGE,"E19.1.0.19"),sQuery(id+"F0.wireOp",EDGE,"E21.1.0.1"),sQuery(id+"F0.wireOp",EDGE,"E21.1.0.2"),sQuery(id+"F0.wireOp",EDGE,"E21.1.0.3"),sQuery(id+"F0.wireOp",EDGE,"E21.1.0.4"),sQuery(id+"F0.wireOp",EDGE,"E21.1.0.5"),sQuery(id+"F0.wireOp",EDGE,"E21.1.0.6"),sQuery(id+"F0.wireOp",EDGE,"E21.1.0.7"),sQuery(id+"F0.wireOp",EDGE,"E21.1.0.8"),sQuery(id+"F0.wireOp",EDGE,"E21.1.0.9"),sQuery(id+"F0.wireOp",EDGE,"E21.1.0.10"),sQuery(id+"F0.wireOp",EDGE,"E21.1.0.11"),sQuery(id+"F0.wireOp",EDGE,"E21.1.0.12"),sQuery(id+"F0.wireOp",EDGE,"E25"),sQuery(id+"F0.wireOp",EDGE,"E26"),sQuery(id+"F0.wireOp",EDGE,"E27"),sQuery(id+"F0.wireOp",EDGE,"E28"),sQuery(id+"F0.wireOp",EDGE,"E29"),sQuery(id+"F0.wireOp",EDGE,"E30"),sQuery(id+"F0.wireOp",EDGE,"E31.1.0.0"),sQuery(id+"F0.wireOp",EDGE,"E31.1.0.1"),sQuery(id+"F0.wireOp",EDGE,"E31.1.0.2"),sQuery(id+"F0.wireOp",EDGE,"E31.1.0.3"),sQuery(id+"F0.wireOp",EDGE,"E31.1.0.4"),sQuery(id+"F0.wireOp",EDGE,"E31.1.0.5"),sQuery(id+"F0.wireOp",EDGE,"E31.2.0.0"),sQuery(id+"F0.wireOp",EDGE,"E31.2.0.1"),sQuery(id+"F0.wireOp",EDGE,"E31.2.0.2"),sQuery(id+"F0.wireOp",EDGE,"E31.2.0.3"),sQuery(id+"F0.wireOp",EDGE,"E31.2.0.4"),sQuery(id+"F0.wireOp",EDGE,"E31.2.0.5"),sQuery(id+"F0.wireOp",EDGE,"E31.3.0.0"),sQuery(id+"F0.wireOp",EDGE,"E31.3.0.1"),sQuery(id+"F0.wireOp",EDGE,"E31.3.0.2"),sQuery(id+"F0.wireOp",EDGE,"E31.3.0.3"),sQuery(id+"F0.wireOp",EDGE,"E31.3.0.4"),sQuery(id+"F0.wireOp",EDGE,"E31.3.0.5"),sQuery(id+"F0.wireOp",EDGE,"E31.4.0.0"),sQuery(id+"F0.wireOp",EDGE,"E31.4.0.1"),sQuery(id+"F0.wireOp",EDGE,"E31.4.0.2"),sQuery(id+"F0.wireOp",EDGE,"E31.4.0.3"),sQuery(id+"F0.wireOp",EDGE,"E31.4.0.4"),sQuery(id+"F0.wireOp",EDGE,"E31.4.0.5"),sQuery(id+"F0.wireOp",EDGE,"E31.5.0.0"),sQuery(id+"F0.wireOp",EDGE,"E31.5.0.1"),sQuery(id+"F0.wireOp",EDGE,"E31.5.0.2"),sQuery(id+"F0.wireOp",EDGE,"E31.5.0.3"),sQuery(id+"F0.wireOp",EDGE,"E31.5.0.4"),sQuery(id+"F0.wireOp",EDGE,"E31.5.0.5"),sQuery(id+"F0.wireOp",EDGE,"E31.6.0.0"),sQuery(id+"F0.wireOp",EDGE,"E31.6.0.1"),sQuery(id+"F0.wireOp",EDGE,"E31.6.0.2"),sQuery(id+"F0.wireOp",EDGE,"E31.6.0.3"),sQuery(id+"F0.wireOp",EDGE,"E31.6.0.4"),sQuery(id+"F0.wireOp",EDGE,"E31.6.0.5"),sQuery(id+"F0.wireOp",EDGE,"E31.7.0.0"),sQuery(id+"F0.wireOp",EDGE,"E31.7.0.1"),sQuery(id+"F0.wireOp",EDGE,"E31.7.0.2"),sQuery(id+"F0.wireOp",EDGE,"E31.7.0.3"),sQuery(id+"F0.wireOp",EDGE,"E31.7.0.4"),sQuery(id+"F0.wireOp",EDGE,"E31.7.0.5"),sQuery(id+"F0.wireOp",EDGE,"E31.8.0.0"),sQuery(id+"F0.wireOp",EDGE,"E31.8.0.1"),sQuery(id+"F0.wireOp",EDGE,"E31.8.0.2"),sQuery(id+"F0.wireOp",EDGE,"E31.8.0.3"),sQuery(id+"F0.wireOp",EDGE,"E31.8.0.4"),sQuery(id+"F0.wireOp",EDGE,"E31.8.0.5"),sQuery(id+"F0.wireOp",EDGE,"E31.9.0.0"),sQuery(id+"F0.wireOp",EDGE,"E31.9.0.1"),sQuery(id+"F0.wireOp",EDGE,"E31.9.0.2"),sQuery(id+"F0.wireOp",EDGE,"E31.9.0.3"),sQuery(id+"F0.wireOp",EDGE,"E31.9.0.4"),sQuery(id+"F0.wireOp",EDGE,"E31.9.0.5"),sQuery(id+"F0.wireOp",EDGE,"E31.10.0.0"),sQuery(id+"F0.wireOp",EDGE,"E31.10.0.1"),sQuery(id+"F0.wireOp",EDGE,"E31.10.0.2"),sQuery(id+"F0.wireOp",EDGE,"E31.10.0.3"),sQuery(id+"F0.wireOp",EDGE,"E31.10.0.4"),sQuery(id+"F0.wireOp",EDGE,"E31.10.0.5"),sQuery(id+"F0.wireOp",EDGE,"E31.11.0.0"),sQuery(id+"F0.wireOp",EDGE,"E31.11.0.1"),sQuery(id+"F0.wireOp",EDGE,"E31.11.0.2"),sQuery(id+"F0.wireOp",EDGE,"E31.11.0.3"),sQuery(id+"F0.wireOp",EDGE,"E31.11.0.4"),sQuery(id+"F0.wireOp",EDGE,"E31.11.0.5"),sQuery(id+"F0.wireOp",EDGE,"E31.12.0.0"),sQuery(id+"F0.wireOp",EDGE,"E31.12.0.1"),sQuery(id+"F0.wireOp",EDGE,"E31.12.0.2"),sQuery(id+"F0.wireOp",EDGE,"E31.12.0.3"),sQuery(id+"F0.wireOp",EDGE,"E31.12.0.4"),sQuery(id+"F0.wireOp",EDGE,"E31.12.0.5"),sQuery(id+"F0.wireOp",EDGE,"E31.13.0.0"),sQuery(id+"F0.wireOp",EDGE,"E31.13.0.1"),sQuery(id+"F0.wireOp",EDGE,"E31.13.0.2"),sQuery(id+"F0.wireOp",EDGE,"E31.13.0.3"),sQuery(id+"F0.wireOp",EDGE,"E31.13.0.4"),sQuery(id+"F0.wireOp",EDGE,"E31.13.0.5"),sQuery(id+"F0.wireOp",EDGE,"E31.14.0.0"),sQuery(id+"F0.wireOp",EDGE,"E31.14.0.1"),sQuery(id+"F0.wireOp",EDGE,"E31.14.0.2"),sQuery(id+"F0.wireOp",EDGE,"E31.14.0.3"),sQuery(id+"F0.wireOp",EDGE,"E31.14.0.4"),sQuery(id+"F0.wireOp",EDGE,"E31.14.0.5"),sQuery(id+"F0.wireOp",EDGE,"E31.15.0.0"),sQuery(id+"F0.wireOp",EDGE,"E31.15.0.1"),sQuery(id+"F0.wireOp",EDGE,"E31.15.0.2"),sQuery(id+"F0.wireOp",EDGE,"E31.15.0.3"),sQuery(id+"F0.wireOp",EDGE,"E31.15.0.4"),sQuery(id+"F0.wireOp",EDGE,"E31.15.0.5"),sQuery(id+"F0.wireOp",EDGE,"E31.16.0.0"),sQuery(id+"F0.wireOp",EDGE,"E31.16.0.1"),sQuery(id+"F0.wireOp",EDGE,"E31.16.0.2"),sQuery(id+"F0.wireOp",EDGE,"E31.16.0.3"),sQuery(id+"F0.wireOp",EDGE,"E31.16.0.4"),sQuery(id+"F0.wireOp",EDGE,"E31.16.0.5"),sQuery(id+"F0.wireOp",EDGE,"E31.17.0.0"),sQuery(id+"F0.wireOp",EDGE,"E31.17.0.1"),sQuery(id+"F0.wireOp",EDGE,"E31.17.0.2"),sQuery(id+"F0.wireOp",EDGE,"E31.17.0.3"),sQuery(id+"F0.wireOp",EDGE,"E31.17.0.4"),sQuery(id+"F0.wireOp",EDGE,"E31.17.0.5"),sQuery(id+"F0.wireOp",EDGE,"E31.18.0.0"),sQuery(id+"F0.wireOp",EDGE,"E31.18.0.1"),sQuery(id+"F0.wireOp",EDGE,"E31.18.0.2"),sQuery(id+"F0.wireOp",EDGE,"E31.18.0.3"),sQuery(id+"F0.wireOp",EDGE,"E31.18.0.4"),sQuery(id+"F0.wireOp",EDGE,"E31.18.0.5"),sQuery(id+"F0.wireOp",EDGE,"E32"),sQuery(id+"F0.wireOp",EDGE,"E33"),sQuery(id+"F0.wireOp",EDGE,"E34"),sQuery(id+"F0.wireOp",EDGE,"E36"),sQuery(id+"F0.wireOp",EDGE,"E37"),sQuery(id+"F0.wireOp",EDGE,"E38"),sQuery(id+"F0.wireOp",EDGE,"E39"),sQuery(id+"F0.wireOp",EDGE,"E40"),sQuery(id+"F0.wireOp",EDGE,"E41"),sQuery(id+"F0.wireOp",EDGE,"E42"),sQuery(id+"F0.wireOp",EDGE,"E43"),sQuery(id+"F0.wireOp",EDGE,"E44"),sQuery(id+"F0.wireOp",EDGE,"E45.bottom"),sQuery(id+"F0.wireOp",EDGE,"E45.top"),sQuery(id+"F0.wireOp",EDGE,"E45.left"),sQuery(id+"F0.wireOp",EDGE,"E45.right"),sQuery(id+"F0.wireOp",EDGE,"E46.bottom"),sQuery(id+"F0.wireOp",EDGE,"E46.top"),sQuery(id+"F0.wireOp",EDGE,"E46.left"),sQuery(id+"F0.wireOp",EDGE,"E46.right"),sQuery(id+"F0.wireOp",EDGE,"E47.bottom"),sQuery(id+"F0.wireOp",EDGE,"E47.top"),sQuery(id+"F0.wireOp",EDGE,"E47.left"),sQuery(id+"F0.wireOp",EDGE,"E47.right"),sQuery(id+"F0.wireOp",EDGE,"E56"),sQuery(id+"F0.wireOp",EDGE,"E57"),sQuery(id+"F0.wireOp",EDGE,"E58"),sQuery(id+"F0.wireOp",EDGE,"E59"),sQuery(id+"F0.wireOp",EDGE,"E60"),sQuery(id+"F0.wireOp",EDGE,"E69"),sQuery(id+"F0.wireOp",EDGE,"E70"),sQuery(id+"F0.wireOp",EDGE,"E71"),sQuery(id+"F0.wireOp",EDGE,"E72"),sQuery(id+"F0.wireOp",EDGE,"E73"),sQuery(id+"F0.wireOp",EDGE,"E79"),sQuery(id+"F0.wireOp",EDGE,"E80"),sQuery(id+"F0.wireOp",EDGE,"E85.bottom"),sQuery(id+"F0.wireOp",EDGE,"E85.top"),sQuery(id+"F0.wireOp",EDGE,"E85.left"),sQuery(id+"F0.wireOp",EDGE,"E85.right"),sQuery(id+"F0.wireOp",EDGE,"E86.bottom"),sQuery(id+"F0.wireOp",EDGE,"E86.top"),sQuery(id+"F0.wireOp",EDGE,"E86.left"),sQuery(id+"F0.wireOp",EDGE,"E86.right"),sQuery(id+"F0.wireOp",EDGE,"E87.bottom"),sQuery(id+"F0.wireOp",EDGE,"E87.top"),sQuery(id+"F0.wireOp",EDGE,"E87.left"),sQuery(id+"F0.wireOp",EDGE,"E87.right"),sQuery(id+"F0.wireOp",EDGE,"E88.bottom"),sQuery(id+"F0.wireOp",EDGE,"E88.top"),sQuery(id+"F0.wireOp",EDGE,"E88.left"),sQuery(id+"F0.wireOp",EDGE,"E88.right"),sQuery(id+"F0.wireOp",EDGE,"E89.bottom"),sQuery(id+"F0.wireOp",EDGE,"E89.top"),sQuery(id+"F0.wireOp",EDGE,"E89.left"),sQuery(id+"F0.wireOp",EDGE,"E89.right"),sQuery(id+"F0.wireOp",EDGE,"E90.bottom"),sQuery(id+"F0.wireOp",EDGE,"E90.top"),sQuery(id+"F0.wireOp",EDGE,"E90.left"),sQuery(id+"F0.wireOp",EDGE,"E90.right"),sQuery(id+"F0.wireOp",EDGE,"E92.bottom"),sQuery(id+"F0.wireOp",EDGE,"E92.top"),sQuery(id+"F0.wireOp",EDGE,"E92.left"),sQuery(id+"F0.wireOp",EDGE,"E92.right"),sQuery(id+"F0.wireOp",EDGE,"E93.bottom"),sQuery(id+"F0.wireOp",EDGE,"E93.top"),sQuery(id+"F0.wireOp",EDGE,"E93.left"),sQuery(id+"F0.wireOp",EDGE,"E93.right")])],"isStart":false});
            var sketch = newSketch(context, id + "F6", { "sketchPlane" : qUnion([Q0])});
            skLineSegment(sketch, "E291.bottom", {"start": v(2.7, 38.24) * mm, "end": v(9, 38.24) * mm});
            skLineSegment(sketch, "E291.top", {"start": v(2.7, 32.34) * mm, "end": v(9, 32.34) * mm});
            skLineSegment(sketch, "E291.left", {"start": v(2.7, 38.24) * mm, "end": v(2.7, 32.34) * mm});
            skLineSegment(sketch, "E291.right", {"start": v(9, 38.24) * mm, "end": v(9, 32.34) * mm});
            skLineSegment(sketch, "E292.bottom", {"start": v(1.7, 11.7) * mm, "end": v(8.5, 11.7) * mm});
            skLineSegment(sketch, "E292.top", {"start": v(1.7, 5.4) * mm, "end": v(8.5, 5.4) * mm});
            skLineSegment(sketch, "E292.left", {"start": v(1.7, 11.7) * mm, "end": v(1.7, 5.4) * mm});
            skLineSegment(sketch, "E292.right", {"start": v(8.5, 11.7) * mm, "end": v(8.5, 5.4) * mm});
            skSolve(sketch);
        }
        {
            var Q0;
            Q0=qSketchRegion(id+"F6",true);
            extrude(context, id + "F7", {"entities" : qUnion([Q0]), "operationType" : NewBodyOperationType.REMOVE, "oppositeDirection" : true, "depth" : 0.2 * mm});
        }
    });
